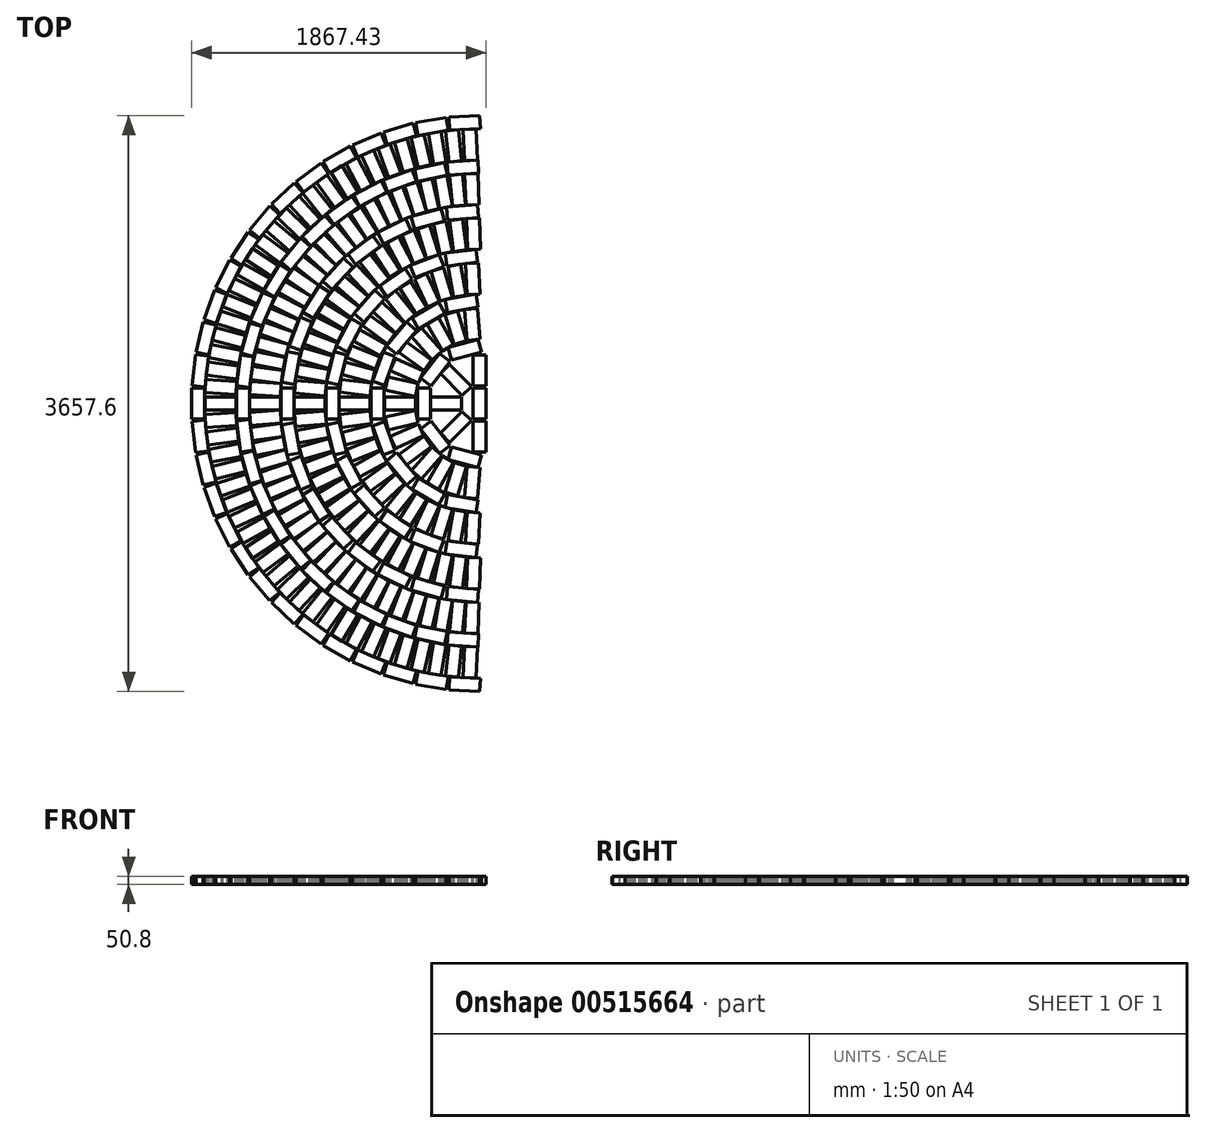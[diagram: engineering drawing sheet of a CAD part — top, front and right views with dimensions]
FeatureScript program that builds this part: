
annotation { "Feature Type Name" : "Feature", "Feature Type Description" : "" }
export const myFeature = defineFeature(function(context is Context, id is Id, definition is map)
    precondition{}
    {
        {
            var Q0;
            Q0=qCreatedBy(makeId("Top.planeOp"),FACE);
            var sketch = newSketch(context, id + "F0", { "sketchPlane" : qUnion([Q0])});
            skArc(sketch, "E0", {"start": v(0, 1828.8) * mm, "mid": v(-1828.8, 0) * mm, "end": v(0, -1828.8) * mm, "construction": true});
            skLineSegment(sketch, "E1", {"start": v(0, 1828.8) * mm, "end": v(0, -1828.8) * mm, "construction": true});
            skCircle(sketch, "E2", {"center": v(-914.4, 0) * mm, "radius": 279.4 * mm, "construction": true});
            skCircle(sketch, "E3", {"center": v(-914.4, 0) * mm, "radius": 609.6 * mm, "construction": true});
            skSolve(sketch);
        }
        {
            var Q0;
            Q0=qCreatedBy(makeId("Top.planeOp"),FACE);
            var sketch = newSketch(context, id + "F1", { "sketchPlane" : qUnion([Q0])});
            skLineSegment(sketch, "E4.bottom", {"start": v(-1826.15, 98.43) * mm, "end": v(-1730.9, 98.43) * mm});
            skLineSegment(sketch, "E4.top", {"start": v(-1826.15, -98.43) * mm, "end": v(-1730.9, -98.43) * mm});
            skLineSegment(sketch, "E4.left", {"start": v(-1826.15, 98.43) * mm, "end": v(-1826.15, -98.43) * mm});
            skLineSegment(sketch, "E4.right", {"start": v(-1730.9, 98.43) * mm, "end": v(-1730.9, -98.43) * mm});
            skLineSegment(sketch, "E5.1.0", {"start": v(-1802.2, 310.84) * mm, "end": v(-1825.16, 115.33) * mm});
            skLineSegment(sketch, "E5.1.1", {"start": v(-1802.2, 310.84) * mm, "end": v(-1707.6, 299.72) * mm});
            skLineSegment(sketch, "E5.1.2", {"start": v(-1707.6, 299.72) * mm, "end": v(-1730.56, 104.22) * mm});
            skLineSegment(sketch, "E5.1.3", {"start": v(-1825.16, 115.33) * mm, "end": v(-1730.56, 104.22) * mm});
            skLineSegment(sketch, "E5.2.0", {"start": v(-1753.6, 519) * mm, "end": v(-1799.23, 327.52) * mm});
            skLineSegment(sketch, "E5.2.1", {"start": v(-1753.6, 519) * mm, "end": v(-1660.95, 496.93) * mm});
            skLineSegment(sketch, "E5.2.2", {"start": v(-1660.95, 496.93) * mm, "end": v(-1706.58, 305.44) * mm});
            skLineSegment(sketch, "E5.2.3", {"start": v(-1799.23, 327.52) * mm, "end": v(-1706.58, 305.44) * mm});
            skLineSegment(sketch, "E5.3.0", {"start": v(-1681.07, 720.08) * mm, "end": v(-1748.73, 535.22) * mm});
            skLineSegment(sketch, "E5.3.1", {"start": v(-1681.07, 720.08) * mm, "end": v(-1591.62, 687.34) * mm});
            skLineSegment(sketch, "E5.3.2", {"start": v(-1591.62, 687.34) * mm, "end": v(-1659.28, 502.49) * mm});
            skLineSegment(sketch, "E5.3.3", {"start": v(-1748.73, 535.22) * mm, "end": v(-1659.28, 502.49) * mm});
            skLineSegment(sketch, "E5.4.0", {"start": v(-1585.56, 911.32) * mm, "end": v(-1674.33, 735.62) * mm});
            skLineSegment(sketch, "E5.4.1", {"start": v(-1585.56, 911.32) * mm, "end": v(-1500.55, 868.37) * mm});
            skLineSegment(sketch, "E5.4.2", {"start": v(-1500.55, 868.37) * mm, "end": v(-1589.31, 692.67) * mm});
            skLineSegment(sketch, "E5.4.3", {"start": v(-1674.33, 735.62) * mm, "end": v(-1589.31, 692.67) * mm});
            skLineSegment(sketch, "E5.5.0", {"start": v(-1468.4, 1090.1) * mm, "end": v(-1577.05, 925.96) * mm});
            skLineSegment(sketch, "E5.5.1", {"start": v(-1468.4, 1090.1) * mm, "end": v(-1388.97, 1037.53) * mm});
            skLineSegment(sketch, "E5.5.2", {"start": v(-1388.97, 1037.53) * mm, "end": v(-1497.63, 873.39) * mm});
            skLineSegment(sketch, "E5.5.3", {"start": v(-1577.05, 925.96) * mm, "end": v(-1497.63, 873.39) * mm});
            skLineSegment(sketch, "E5.6.0", {"start": v(-1331.16, 1254) * mm, "end": v(-1458.23, 1103.66) * mm});
            skLineSegment(sketch, "E5.6.1", {"start": v(-1331.16, 1254) * mm, "end": v(-1258.42, 1192.51) * mm});
            skLineSegment(sketch, "E5.6.2", {"start": v(-1258.42, 1192.51) * mm, "end": v(-1385.49, 1042.17) * mm});
            skLineSegment(sketch, "E5.6.3", {"start": v(-1458.23, 1103.66) * mm, "end": v(-1385.49, 1042.17) * mm});
            skLineSegment(sketch, "E5.7.0", {"start": v(-1175.75, 1400.76) * mm, "end": v(-1319.5, 1266.27) * mm});
            skLineSegment(sketch, "E5.7.1", {"start": v(-1175.75, 1400.76) * mm, "end": v(-1110.67, 1331.2) * mm});
            skLineSegment(sketch, "E5.7.2", {"start": v(-1110.67, 1331.2) * mm, "end": v(-1254.42, 1196.72) * mm});
            skLineSegment(sketch, "E5.7.3", {"start": v(-1319.5, 1266.27) * mm, "end": v(-1254.42, 1196.72) * mm});
            skLineSegment(sketch, "E5.8.0", {"start": v(-1004.27, 1528.38) * mm, "end": v(-1162.72, 1411.59) * mm});
            skLineSegment(sketch, "E5.8.1", {"start": v(-1004.27, 1528.38) * mm, "end": v(-947.75, 1451.71) * mm});
            skLineSegment(sketch, "E5.8.2", {"start": v(-947.75, 1451.71) * mm, "end": v(-1106.2, 1334.92) * mm});
            skLineSegment(sketch, "E5.8.3", {"start": v(-1162.72, 1411.59) * mm, "end": v(-1106.2, 1334.92) * mm});
            skLineSegment(sketch, "E5.9.0", {"start": v(-819.06, 1635.13) * mm, "end": v(-990.07, 1537.62) * mm});
            skLineSegment(sketch, "E5.9.1", {"start": v(-819.06, 1635.13) * mm, "end": v(-771.88, 1552.38) * mm});
            skLineSegment(sketch, "E5.9.2", {"start": v(-771.88, 1552.38) * mm, "end": v(-942.89, 1454.88) * mm});
            skLineSegment(sketch, "E5.9.3", {"start": v(-990.07, 1537.62) * mm, "end": v(-942.89, 1454.88) * mm});
            skLineSegment(sketch, "E5.10.0", {"start": v(-622.67, 1719.53) * mm, "end": v(-803.89, 1642.64) * mm});
            skLineSegment(sketch, "E5.10.1", {"start": v(-622.67, 1719.53) * mm, "end": v(-585.47, 1631.85) * mm});
            skLineSegment(sketch, "E5.10.2", {"start": v(-585.47, 1631.85) * mm, "end": v(-766.68, 1554.96) * mm});
            skLineSegment(sketch, "E5.10.3", {"start": v(-803.89, 1642.64) * mm, "end": v(-766.68, 1554.96) * mm});
            skLineSegment(sketch, "E5.11.0", {"start": v(-417.78, 1780.44) * mm, "end": v(-606.72, 1725.22) * mm});
            skLineSegment(sketch, "E5.11.1", {"start": v(-417.78, 1780.44) * mm, "end": v(-391.06, 1689.02) * mm});
            skLineSegment(sketch, "E5.11.2", {"start": v(-391.06, 1689.02) * mm, "end": v(-580, 1633.8) * mm});
            skLineSegment(sketch, "E5.11.3", {"start": v(-606.72, 1725.22) * mm, "end": v(-580, 1633.8) * mm});
            skLineSegment(sketch, "E5.12.0", {"start": v(-207.17, 1817.03) * mm, "end": v(-401.27, 1784.23) * mm});
            skLineSegment(sketch, "E5.12.1", {"start": v(-207.17, 1817.03) * mm, "end": v(-191.3, 1723.1) * mm});
            skLineSegment(sketch, "E5.12.2", {"start": v(-191.3, 1723.1) * mm, "end": v(-385.4, 1690.32) * mm});
            skLineSegment(sketch, "E5.12.3", {"start": v(-401.27, 1784.23) * mm, "end": v(-385.4, 1690.32) * mm});
            skLineSegment(sketch, "E5.13.0", {"start": v(6.27, 1828.79) * mm, "end": v(-190.33, 1818.87) * mm});
            skLineSegment(sketch, "E5.13.1", {"start": v(6.27, 1828.79) * mm, "end": v(11.07, 1733.66) * mm});
            skLineSegment(sketch, "E5.13.2", {"start": v(11.07, 1733.66) * mm, "end": v(-185.53, 1723.74) * mm});
            skLineSegment(sketch, "E5.13.3", {"start": v(-190.33, 1818.87) * mm, "end": v(-185.53, 1723.74) * mm});
            skPoint(sketch, "E5.center", {"position": v(0, 0) * mm});
            skLineSegment(sketch, "E5.anchor1", {"start": v(0, 0) * mm, "end": v(-1826.15, -98.43) * mm, "construction": true});
            skLineSegment(sketch, "E5.anchor2", {"start": v(0, 0) * mm, "end": v(-190.33, 1818.87) * mm, "construction": true});
            skLineSegment(sketch, "E6.MirrorCS", {"start": v(-1825.16, -115.33) * mm, "end": v(-1730.56, -104.22) * mm});
            skLineSegment(sketch, "E7.MirrorCS", {"start": v(-1802.2, -310.84) * mm, "end": v(-1825.16, -115.33) * mm});
            skLineSegment(sketch, "E8.MirrorCS", {"start": v(-1802.2, -310.84) * mm, "end": v(-1707.6, -299.72) * mm});
            skLineSegment(sketch, "E9.MirrorCS", {"start": v(-1707.6, -299.72) * mm, "end": v(-1730.56, -104.22) * mm});
            skLineSegment(sketch, "E10.MirrorCS", {"start": v(-190.33, -1818.87) * mm, "end": v(-185.53, -1723.74) * mm});
            skLineSegment(sketch, "E11.MirrorCS", {"start": v(-1826.15, -98.43) * mm, "end": v(-1826.15, 98.43) * mm});
            skLineSegment(sketch, "E12.MirrorCS", {"start": v(-1730.9, -98.43) * mm, "end": v(-1730.9, 98.43) * mm});
            skLineSegment(sketch, "E13.MirrorCS", {"start": v(-803.89, -1642.64) * mm, "end": v(-766.68, -1554.96) * mm});
            skLineSegment(sketch, "E14.MirrorCS", {"start": v(-990.07, -1537.62) * mm, "end": v(-942.89, -1454.88) * mm});
            skLineSegment(sketch, "E15.MirrorCS", {"start": v(-1681.07, -720.08) * mm, "end": v(-1591.62, -687.34) * mm});
            skLineSegment(sketch, "E16.MirrorCS", {"start": v(-1748.73, -535.22) * mm, "end": v(-1659.28, -502.49) * mm});
            skLineSegment(sketch, "E17.MirrorCS", {"start": v(-819.06, -1635.13) * mm, "end": v(-771.88, -1552.38) * mm});
            skLineSegment(sketch, "E18.MirrorCS", {"start": v(-191.3, -1723.1) * mm, "end": v(-385.4, -1690.32) * mm});
            skLineSegment(sketch, "E19.MirrorCS", {"start": v(-1458.23, -1103.66) * mm, "end": v(-1385.49, -1042.17) * mm});
            skLineSegment(sketch, "E20.MirrorCS", {"start": v(-207.17, -1817.03) * mm, "end": v(-191.3, -1723.1) * mm});
            skLineSegment(sketch, "E21.MirrorCS", {"start": v(-1175.75, -1400.76) * mm, "end": v(-1110.67, -1331.2) * mm});
            skLineSegment(sketch, "E22.MirrorCS", {"start": v(6.27, -1828.79) * mm, "end": v(-190.33, -1818.87) * mm});
            skLineSegment(sketch, "E23.MirrorCS", {"start": v(-1577.05, -925.96) * mm, "end": v(-1497.63, -873.39) * mm});
            skLineSegment(sketch, "E24.MirrorCS", {"start": v(-207.17, -1817.03) * mm, "end": v(-401.27, -1784.23) * mm});
            skLineSegment(sketch, "E25.MirrorCS", {"start": v(-606.72, -1725.22) * mm, "end": v(-580, -1633.8) * mm});
            skLineSegment(sketch, "E26.MirrorCS", {"start": v(-1004.27, -1528.38) * mm, "end": v(-1162.72, -1411.59) * mm});
            skLineSegment(sketch, "E27.MirrorCS", {"start": v(-1585.56, -911.32) * mm, "end": v(-1674.33, -735.62) * mm});
            skLineSegment(sketch, "E28.MirrorCS", {"start": v(-1331.16, -1254) * mm, "end": v(-1258.42, -1192.51) * mm});
            skLineSegment(sketch, "E29.MirrorCS", {"start": v(-1591.62, -687.34) * mm, "end": v(-1659.28, -502.49) * mm});
            skLineSegment(sketch, "E30.MirrorCS", {"start": v(-1468.4, -1090.1) * mm, "end": v(-1388.97, -1037.53) * mm});
            skLineSegment(sketch, "E31.MirrorCS", {"start": v(-1110.67, -1331.2) * mm, "end": v(-1254.42, -1196.72) * mm});
            skLineSegment(sketch, "E32.MirrorCS", {"start": v(-1331.16, -1254) * mm, "end": v(-1458.23, -1103.66) * mm});
            skLineSegment(sketch, "E33.MirrorCS", {"start": v(-1500.55, -868.37) * mm, "end": v(-1589.31, -692.67) * mm});
            skLineSegment(sketch, "E34.MirrorCS", {"start": v(-947.75, -1451.71) * mm, "end": v(-1106.2, -1334.92) * mm});
            skLineSegment(sketch, "E35.MirrorCS", {"start": v(-622.67, -1719.53) * mm, "end": v(-585.47, -1631.85) * mm});
            skLineSegment(sketch, "E36.MirrorCS", {"start": v(-1319.5, -1266.27) * mm, "end": v(-1254.42, -1196.72) * mm});
            skLineSegment(sketch, "E37.MirrorCS", {"start": v(-1388.97, -1037.53) * mm, "end": v(-1497.63, -873.39) * mm});
            skLineSegment(sketch, "E38.MirrorCS", {"start": v(-1258.42, -1192.51) * mm, "end": v(-1385.49, -1042.17) * mm});
            skLineSegment(sketch, "E39.MirrorCS", {"start": v(-585.47, -1631.85) * mm, "end": v(-766.68, -1554.96) * mm});
            skLineSegment(sketch, "E40.MirrorCS", {"start": v(-1799.23, -327.52) * mm, "end": v(-1706.58, -305.44) * mm});
            skLineSegment(sketch, "E41.MirrorCS", {"start": v(-771.88, -1552.38) * mm, "end": v(-942.89, -1454.88) * mm});
            skLineSegment(sketch, "E42.MirrorCS", {"start": v(-417.78, -1780.44) * mm, "end": v(-391.06, -1689.02) * mm});
            skLineSegment(sketch, "E43.MirrorCS", {"start": v(-1660.95, -496.93) * mm, "end": v(-1706.58, -305.44) * mm});
            skLineSegment(sketch, "E44.MirrorCS", {"start": v(-1468.4, -1090.1) * mm, "end": v(-1577.05, -925.96) * mm});
            skLineSegment(sketch, "E45.MirrorCS", {"start": v(-1753.6, -519) * mm, "end": v(-1660.95, -496.93) * mm});
            skLineSegment(sketch, "E46.MirrorCS", {"start": v(-819.06, -1635.13) * mm, "end": v(-990.07, -1537.62) * mm});
            skLineSegment(sketch, "E47.MirrorCS", {"start": v(-1162.72, -1411.59) * mm, "end": v(-1106.2, -1334.92) * mm});
            skLineSegment(sketch, "E48.MirrorCS", {"start": v(-1681.07, -720.08) * mm, "end": v(-1748.73, -535.22) * mm});
            skLineSegment(sketch, "E49.MirrorCS", {"start": v(-1674.33, -735.62) * mm, "end": v(-1589.31, -692.67) * mm});
            skLineSegment(sketch, "E50.MirrorCS", {"start": v(-1753.6, -519) * mm, "end": v(-1799.23, -327.52) * mm});
            skLineSegment(sketch, "E51.MirrorCS", {"start": v(-1175.75, -1400.76) * mm, "end": v(-1319.5, -1266.27) * mm});
            skLineSegment(sketch, "E52.MirrorCS", {"start": v(-1585.56, -911.32) * mm, "end": v(-1500.55, -868.37) * mm});
            skLineSegment(sketch, "E53.MirrorCS", {"start": v(-417.78, -1780.44) * mm, "end": v(-606.72, -1725.22) * mm});
            skLineSegment(sketch, "E54.MirrorCS", {"start": v(-1004.27, -1528.38) * mm, "end": v(-947.75, -1451.71) * mm});
            skLineSegment(sketch, "E55.MirrorCS", {"start": v(6.27, -1828.79) * mm, "end": v(11.07, -1733.66) * mm});
            skLineSegment(sketch, "E56.MirrorCS", {"start": v(-622.67, -1719.53) * mm, "end": v(-803.89, -1642.64) * mm});
            skLineSegment(sketch, "E57.MirrorCS", {"start": v(-401.27, -1784.23) * mm, "end": v(-385.4, -1690.32) * mm});
            skLineSegment(sketch, "E58.MirrorCS", {"start": v(-391.06, -1689.02) * mm, "end": v(-580, -1633.8) * mm});
            skLineSegment(sketch, "E59.MirrorCS", {"start": v(11.07, -1733.66) * mm, "end": v(-185.53, -1723.74) * mm});
            skLineSegment(sketch, "E60.MirrorCS", {"start": v(0, 0) * mm, "end": v(-190.33, -1818.87) * mm, "construction": true});
            skSolve(sketch);
        }
        {
            var Q0;
            Q0=qCreatedBy(makeId("Top.planeOp"),FACE);
            var sketch = newSketch(context, id + "F2", { "sketchPlane" : qUnion([Q0])});
            skCircle(sketch, "E61", {"center": v(0, 0) * mm, "radius": 1730.9 * mm, "construction": true});
            skLineSegment(sketch, "E62.bottom", {"start": v(-1730.24, 47.63) * mm, "end": v(-1533.4, 47.63) * mm});
            skLineSegment(sketch, "E62.top", {"start": v(-1730.24, -47.63) * mm, "end": v(-1533.4, -47.63) * mm});
            skLineSegment(sketch, "E62.left", {"start": v(-1730.24, 47.63) * mm, "end": v(-1730.24, -47.63) * mm});
            skLineSegment(sketch, "E62.right", {"start": v(-1533.4, 47.63) * mm, "end": v(-1533.4, -47.63) * mm});
            skLineSegment(sketch, "E63.1.0", {"start": v(-1723.66, 158.1) * mm, "end": v(-1527.22, 145.51) * mm});
            skLineSegment(sketch, "E63.1.1", {"start": v(-1527.22, 145.51) * mm, "end": v(-1533.3, 50.46) * mm});
            skLineSegment(sketch, "E63.1.2", {"start": v(-1729.75, 63.04) * mm, "end": v(-1533.3, 50.46) * mm});
            skLineSegment(sketch, "E63.1.3", {"start": v(-1723.66, 158.1) * mm, "end": v(-1729.75, 63.04) * mm});
            skLineSegment(sketch, "E63.2.0", {"start": v(-1710.04, 267.92) * mm, "end": v(-1514.8, 242.8) * mm});
            skLineSegment(sketch, "E63.2.1", {"start": v(-1514.8, 242.8) * mm, "end": v(-1526.95, 148.34) * mm});
            skLineSegment(sketch, "E63.2.2", {"start": v(-1722.19, 173.44) * mm, "end": v(-1526.95, 148.34) * mm});
            skLineSegment(sketch, "E63.2.3", {"start": v(-1710.04, 267.92) * mm, "end": v(-1722.19, 173.44) * mm});
            skLineSegment(sketch, "E63.3.0", {"start": v(-1689.42, 376.64) * mm, "end": v(-1496.18, 339.11) * mm});
            skLineSegment(sketch, "E63.3.1", {"start": v(-1496.18, 339.11) * mm, "end": v(-1514.35, 245.6) * mm});
            skLineSegment(sketch, "E63.3.2", {"start": v(-1707.58, 283.14) * mm, "end": v(-1514.35, 245.6) * mm});
            skLineSegment(sketch, "E63.3.3", {"start": v(-1689.42, 376.64) * mm, "end": v(-1707.58, 283.14) * mm});
            skLineSegment(sketch, "E63.4.0", {"start": v(-1661.9, 483.83) * mm, "end": v(-1471.46, 434.03) * mm});
            skLineSegment(sketch, "E63.4.1", {"start": v(-1471.46, 434.03) * mm, "end": v(-1495.56, 341.88) * mm});
            skLineSegment(sketch, "E63.4.2", {"start": v(-1686, 391.68) * mm, "end": v(-1495.56, 341.88) * mm});
            skLineSegment(sketch, "E63.4.3", {"start": v(-1661.9, 483.83) * mm, "end": v(-1686, 391.68) * mm});
            skLineSegment(sketch, "E63.5.0", {"start": v(-1627.59, 589.04) * mm, "end": v(-1440.71, 527.17) * mm});
            skLineSegment(sketch, "E63.5.1", {"start": v(-1440.71, 527.17) * mm, "end": v(-1470.65, 436.75) * mm});
            skLineSegment(sketch, "E63.5.2", {"start": v(-1657.53, 498.62) * mm, "end": v(-1470.65, 436.75) * mm});
            skLineSegment(sketch, "E63.5.3", {"start": v(-1627.59, 589.04) * mm, "end": v(-1657.53, 498.62) * mm});
            skLineSegment(sketch, "E63.6.0", {"start": v(-1586.62, 691.84) * mm, "end": v(-1404.08, 618.16) * mm});
            skLineSegment(sketch, "E63.6.1", {"start": v(-1404.08, 618.16) * mm, "end": v(-1439.74, 529.83) * mm});
            skLineSegment(sketch, "E63.6.2", {"start": v(-1622.28, 603.52) * mm, "end": v(-1439.74, 529.83) * mm});
            skLineSegment(sketch, "E63.6.3", {"start": v(-1586.62, 691.84) * mm, "end": v(-1622.28, 603.52) * mm});
            skLineSegment(sketch, "E63.7.0", {"start": v(-1539.17, 791.82) * mm, "end": v(-1361.71, 706.62) * mm});
            skLineSegment(sketch, "E63.7.1", {"start": v(-1361.71, 706.62) * mm, "end": v(-1402.94, 620.75) * mm});
            skLineSegment(sketch, "E63.7.2", {"start": v(-1580.4, 705.95) * mm, "end": v(-1402.94, 620.75) * mm});
            skLineSegment(sketch, "E63.7.3", {"start": v(-1539.17, 791.82) * mm, "end": v(-1580.4, 705.95) * mm});
            skLineSegment(sketch, "E63.8.0", {"start": v(-1485.42, 888.55) * mm, "end": v(-1313.77, 792.19) * mm});
            skLineSegment(sketch, "E63.8.1", {"start": v(-1313.77, 792.19) * mm, "end": v(-1360.4, 709.13) * mm});
            skLineSegment(sketch, "E63.8.2", {"start": v(-1532.05, 805.5) * mm, "end": v(-1360.4, 709.13) * mm});
            skLineSegment(sketch, "E63.8.3", {"start": v(-1485.42, 888.55) * mm, "end": v(-1532.05, 805.5) * mm});
            skLineSegment(sketch, "E63.9.0", {"start": v(-1425.6, 981.66) * mm, "end": v(-1260.47, 874.52) * mm});
            skLineSegment(sketch, "E63.9.1", {"start": v(-1260.47, 874.52) * mm, "end": v(-1312.3, 794.62) * mm});
            skLineSegment(sketch, "E63.9.2", {"start": v(-1477.45, 901.75) * mm, "end": v(-1312.3, 794.62) * mm});
            skLineSegment(sketch, "E63.9.3", {"start": v(-1425.6, 981.66) * mm, "end": v(-1477.45, 901.75) * mm});
            skLineSegment(sketch, "E63.10.0", {"start": v(-1359.96, 1070.75) * mm, "end": v(-1202, 953.28) * mm});
            skLineSegment(sketch, "E63.10.1", {"start": v(-1202, 953.28) * mm, "end": v(-1258.85, 876.85) * mm});
            skLineSegment(sketch, "E63.10.2", {"start": v(-1416.8, 994.32) * mm, "end": v(-1258.85, 876.85) * mm});
            skLineSegment(sketch, "E63.10.3", {"start": v(-1359.96, 1070.75) * mm, "end": v(-1416.8, 994.32) * mm});
            skLineSegment(sketch, "E63.11.0", {"start": v(-1288.76, 1155.47) * mm, "end": v(-1138.63, 1028.14) * mm});
            skLineSegment(sketch, "E63.11.1", {"start": v(-1138.63, 1028.14) * mm, "end": v(-1200.24, 955.5) * mm});
            skLineSegment(sketch, "E63.11.2", {"start": v(-1350.37, 1082.83) * mm, "end": v(-1200.24, 955.5) * mm});
            skLineSegment(sketch, "E63.11.3", {"start": v(-1288.76, 1155.47) * mm, "end": v(-1350.37, 1082.83) * mm});
            skLineSegment(sketch, "E63.12.0", {"start": v(-1212.3, 1235.46) * mm, "end": v(-1070.6, 1098.8) * mm});
            skLineSegment(sketch, "E63.12.1", {"start": v(-1070.6, 1098.8) * mm, "end": v(-1136.73, 1030.25) * mm});
            skLineSegment(sketch, "E63.12.2", {"start": v(-1278.42, 1166.9) * mm, "end": v(-1136.73, 1030.25) * mm});
            skLineSegment(sketch, "E63.12.3", {"start": v(-1212.3, 1235.46) * mm, "end": v(-1278.42, 1166.9) * mm});
            skLineSegment(sketch, "E63.13.0", {"start": v(-1130.86, 1310.4) * mm, "end": v(-998.2, 1164.97) * mm});
            skLineSegment(sketch, "E63.13.1", {"start": v(-998.2, 1164.97) * mm, "end": v(-1068.57, 1100.78) * mm});
            skLineSegment(sketch, "E63.13.2", {"start": v(-1201.24, 1246.21) * mm, "end": v(-1068.57, 1100.78) * mm});
            skLineSegment(sketch, "E63.13.3", {"start": v(-1130.86, 1310.4) * mm, "end": v(-1201.24, 1246.21) * mm});
            skLineSegment(sketch, "E63.14.0", {"start": v(-1044.82, 1380) * mm, "end": v(-921.72, 1226.38) * mm});
            skLineSegment(sketch, "E63.14.1", {"start": v(-921.72, 1226.38) * mm, "end": v(-996.05, 1166.81) * mm});
            skLineSegment(sketch, "E63.14.2", {"start": v(-1119.14, 1320.43) * mm, "end": v(-996.05, 1166.81) * mm});
            skLineSegment(sketch, "E63.14.3", {"start": v(-1044.82, 1380) * mm, "end": v(-1119.14, 1320.43) * mm});
            skLineSegment(sketch, "E63.15.0", {"start": v(-954.5, 1443.94) * mm, "end": v(-841.47, 1282.77) * mm});
            skLineSegment(sketch, "E63.15.1", {"start": v(-841.47, 1282.77) * mm, "end": v(-919.45, 1228.08) * mm});
            skLineSegment(sketch, "E63.15.2", {"start": v(-1032.48, 1389.24) * mm, "end": v(-919.45, 1228.08) * mm});
            skLineSegment(sketch, "E63.15.3", {"start": v(-954.5, 1443.94) * mm, "end": v(-1032.48, 1389.24) * mm});
            skLineSegment(sketch, "E63.16.0", {"start": v(-860.27, 1501.98) * mm, "end": v(-757.78, 1333.92) * mm});
            skLineSegment(sketch, "E63.16.1", {"start": v(-757.78, 1333.92) * mm, "end": v(-839.1, 1284.32) * mm});
            skLineSegment(sketch, "E63.16.2", {"start": v(-941.6, 1452.38) * mm, "end": v(-839.1, 1284.32) * mm});
            skLineSegment(sketch, "E63.16.3", {"start": v(-860.27, 1501.98) * mm, "end": v(-941.6, 1452.38) * mm});
            skLineSegment(sketch, "E63.17.0", {"start": v(-762.54, 1553.88) * mm, "end": v(-670.99, 1379.62) * mm});
            skLineSegment(sketch, "E63.17.1", {"start": v(-670.99, 1379.62) * mm, "end": v(-755.3, 1335.32) * mm});
            skLineSegment(sketch, "E63.17.2", {"start": v(-846.86, 1509.58) * mm, "end": v(-755.3, 1335.32) * mm});
            skLineSegment(sketch, "E63.17.3", {"start": v(-762.54, 1553.88) * mm, "end": v(-846.86, 1509.58) * mm});
            skLineSegment(sketch, "E63.18.0", {"start": v(-661.68, 1599.43) * mm, "end": v(-581.46, 1419.67) * mm});
            skLineSegment(sketch, "E63.18.1", {"start": v(-581.46, 1419.67) * mm, "end": v(-668.44, 1380.85) * mm});
            skLineSegment(sketch, "E63.18.2", {"start": v(-748.66, 1560.61) * mm, "end": v(-668.44, 1380.85) * mm});
            skLineSegment(sketch, "E63.18.3", {"start": v(-661.68, 1599.43) * mm, "end": v(-748.66, 1560.61) * mm});
            skLineSegment(sketch, "E63.19.0", {"start": v(-558.12, 1638.45) * mm, "end": v(-489.55, 1453.93) * mm});
            skLineSegment(sketch, "E63.19.1", {"start": v(-489.55, 1453.93) * mm, "end": v(-578.83, 1420.75) * mm});
            skLineSegment(sketch, "E63.19.2", {"start": v(-647.4, 1605.27) * mm, "end": v(-578.83, 1420.75) * mm});
            skLineSegment(sketch, "E63.19.3", {"start": v(-558.12, 1638.45) * mm, "end": v(-647.4, 1605.27) * mm});
            skLineSegment(sketch, "E63.20.0", {"start": v(-452.28, 1670.76) * mm, "end": v(-395.64, 1482.24) * mm});
            skLineSegment(sketch, "E63.20.1", {"start": v(-395.64, 1482.24) * mm, "end": v(-486.86, 1454.83) * mm});
            skLineSegment(sketch, "E63.20.2", {"start": v(-543.5, 1643.36) * mm, "end": v(-486.86, 1454.83) * mm});
            skLineSegment(sketch, "E63.20.3", {"start": v(-452.28, 1670.76) * mm, "end": v(-543.5, 1643.36) * mm});
            skLineSegment(sketch, "E63.21.0", {"start": v(-344.6, 1696.25) * mm, "end": v(-300.11, 1504.5) * mm});
            skLineSegment(sketch, "E63.21.1", {"start": v(-300.11, 1504.5) * mm, "end": v(-392.9, 1482.97) * mm});
            skLineSegment(sketch, "E63.21.2", {"start": v(-437.38, 1674.73) * mm, "end": v(-392.9, 1482.97) * mm});
            skLineSegment(sketch, "E63.21.3", {"start": v(-344.6, 1696.25) * mm, "end": v(-437.38, 1674.73) * mm});
            skLineSegment(sketch, "E63.22.0", {"start": v(-235.5, 1714.8) * mm, "end": v(-203.36, 1520.6) * mm});
            skLineSegment(sketch, "E63.22.1", {"start": v(-203.36, 1520.6) * mm, "end": v(-297.33, 1505.05) * mm});
            skLineSegment(sketch, "E63.22.2", {"start": v(-329.47, 1699.25) * mm, "end": v(-297.33, 1505.05) * mm});
            skLineSegment(sketch, "E63.22.3", {"start": v(-235.5, 1714.8) * mm, "end": v(-329.47, 1699.25) * mm});
            skLineSegment(sketch, "E63.23.0", {"start": v(-125.43, 1726.35) * mm, "end": v(-105.77, 1530.48) * mm});
            skLineSegment(sketch, "E63.23.1", {"start": v(-105.77, 1530.48) * mm, "end": v(-200.55, 1520.97) * mm});
            skLineSegment(sketch, "E63.23.2", {"start": v(-220.2, 1716.83) * mm, "end": v(-200.55, 1520.97) * mm});
            skLineSegment(sketch, "E63.23.3", {"start": v(-125.43, 1726.35) * mm, "end": v(-220.2, 1716.83) * mm});
            skLineSegment(sketch, "E63.24.0", {"start": v(-14.86, 1730.84) * mm, "end": v(-7.76, 1534.11) * mm});
            skLineSegment(sketch, "E63.24.1", {"start": v(-7.76, 1534.11) * mm, "end": v(-102.94, 1530.68) * mm});
            skLineSegment(sketch, "E63.24.2", {"start": v(-110.05, 1727.4) * mm, "end": v(-102.94, 1530.68) * mm});
            skLineSegment(sketch, "E63.24.3", {"start": v(-14.86, 1730.84) * mm, "end": v(-110.05, 1727.4) * mm});
            skLineSegment(sketch, "E63.anchor1", {"start": v(0, 0) * mm, "end": v(-1730.24, 47.63) * mm, "construction": true});
            skLineSegment(sketch, "E63.anchor2", {"start": v(0, 0) * mm, "end": v(-14.86, 1730.84) * mm, "construction": true});
            skLineSegment(sketch, "E64.MirrorCS", {"start": v(-1729.75, -63.04) * mm, "end": v(-1533.3, -50.46) * mm});
            skLineSegment(sketch, "E65.MirrorCS", {"start": v(-1723.66, -158.1) * mm, "end": v(-1729.75, -63.04) * mm});
            skLineSegment(sketch, "E66.MirrorCS", {"start": v(-1723.66, -158.1) * mm, "end": v(-1527.22, -145.51) * mm});
            skLineSegment(sketch, "E67.MirrorCS", {"start": v(-1527.22, -145.51) * mm, "end": v(-1533.3, -50.46) * mm});
            skLineSegment(sketch, "E68.MirrorCS", {"start": v(-1359.96, -1070.75) * mm, "end": v(-1416.8, -994.32) * mm});
            skLineSegment(sketch, "E69.MirrorCS", {"start": v(-1361.71, -706.62) * mm, "end": v(-1402.94, -620.75) * mm});
            skLineSegment(sketch, "E70.MirrorCS", {"start": v(-1425.6, -981.66) * mm, "end": v(-1260.47, -874.52) * mm});
            skLineSegment(sketch, "E71.MirrorCS", {"start": v(-105.77, -1530.48) * mm, "end": v(-200.55, -1520.97) * mm});
            skLineSegment(sketch, "E72.MirrorCS", {"start": v(-1440.71, -527.17) * mm, "end": v(-1470.65, -436.75) * mm});
            skLineSegment(sketch, "E73.MirrorCS", {"start": v(-300.11, -1504.5) * mm, "end": v(-392.9, -1482.97) * mm});
            skLineSegment(sketch, "E74.MirrorCS", {"start": v(-670.99, -1379.62) * mm, "end": v(-755.3, -1335.32) * mm});
            skLineSegment(sketch, "E75.MirrorCS", {"start": v(-998.2, -1164.97) * mm, "end": v(-1068.57, -1100.78) * mm});
            skLineSegment(sketch, "E76.MirrorCS", {"start": v(-1260.47, -874.52) * mm, "end": v(-1312.3, -794.62) * mm});
            skLineSegment(sketch, "E77.MirrorCS", {"start": v(-1539.17, -791.82) * mm, "end": v(-1580.4, -705.95) * mm});
            skLineSegment(sketch, "E78.MirrorCS", {"start": v(-125.43, -1726.35) * mm, "end": v(-220.2, -1716.83) * mm});
            skLineSegment(sketch, "E79.MirrorCS", {"start": v(-1689.42, -376.64) * mm, "end": v(-1707.58, -283.14) * mm});
            skLineSegment(sketch, "E80.MirrorCS", {"start": v(-1425.6, -981.66) * mm, "end": v(-1477.45, -901.75) * mm});
            skLineSegment(sketch, "E81.MirrorCS", {"start": v(-1496.18, -339.11) * mm, "end": v(-1514.35, -245.6) * mm});
            skLineSegment(sketch, "E82.MirrorCS", {"start": v(-1471.46, -434.03) * mm, "end": v(-1495.56, -341.88) * mm});
            skLineSegment(sketch, "E83.MirrorCS", {"start": v(-757.78, -1333.92) * mm, "end": v(-839.1, -1284.32) * mm});
            skLineSegment(sketch, "E84.MirrorCS", {"start": v(-1313.77, -792.19) * mm, "end": v(-1360.4, -709.13) * mm});
            skLineSegment(sketch, "E85.MirrorCS", {"start": v(-1514.8, -242.8) * mm, "end": v(-1526.95, -148.34) * mm});
            skLineSegment(sketch, "E86.MirrorCS", {"start": v(-1404.08, -618.16) * mm, "end": v(-1439.74, -529.83) * mm});
            skLineSegment(sketch, "E87.MirrorCS", {"start": v(-203.36, -1520.6) * mm, "end": v(-297.33, -1505.05) * mm});
            skLineSegment(sketch, "E88.MirrorCS", {"start": v(-581.46, -1419.67) * mm, "end": v(-668.44, -1380.85) * mm});
            skLineSegment(sketch, "E89.MirrorCS", {"start": v(-1661.9, -483.83) * mm, "end": v(-1686, -391.68) * mm});
            skLineSegment(sketch, "E90.MirrorCS", {"start": v(-1212.3, -1235.46) * mm, "end": v(-1278.42, -1166.9) * mm});
            skLineSegment(sketch, "E91.MirrorCS", {"start": v(-1485.42, -888.55) * mm, "end": v(-1532.05, -805.5) * mm});
            skLineSegment(sketch, "E92.MirrorCS", {"start": v(-14.86, -1730.84) * mm, "end": v(-110.05, -1727.4) * mm});
            skLineSegment(sketch, "E93.MirrorCS", {"start": v(-1201.24, -1246.21) * mm, "end": v(-1068.57, -1100.78) * mm});
            skLineSegment(sketch, "E94.MirrorCS", {"start": v(-1044.82, -1380) * mm, "end": v(-1119.14, -1320.43) * mm});
            skLineSegment(sketch, "E95.MirrorCS", {"start": v(-1586.62, -691.84) * mm, "end": v(-1622.28, -603.52) * mm});
            skLineSegment(sketch, "E96.MirrorCS", {"start": v(-235.5, -1714.8) * mm, "end": v(-329.47, -1699.25) * mm});
            skLineSegment(sketch, "E97.MirrorCS", {"start": v(-661.68, -1599.43) * mm, "end": v(-748.66, -1560.61) * mm});
            skLineSegment(sketch, "E98.MirrorCS", {"start": v(-489.55, -1453.93) * mm, "end": v(-578.83, -1420.75) * mm});
            skLineSegment(sketch, "E99.MirrorCS", {"start": v(-841.47, -1282.77) * mm, "end": v(-919.45, -1228.08) * mm});
            skLineSegment(sketch, "E100.MirrorCS", {"start": v(-1138.63, -1028.14) * mm, "end": v(-1200.24, -955.5) * mm});
            skLineSegment(sketch, "E101.MirrorCS", {"start": v(-558.12, -1638.45) * mm, "end": v(-647.4, -1605.27) * mm});
            skLineSegment(sketch, "E102.MirrorCS", {"start": v(-954.5, -1443.94) * mm, "end": v(-1032.48, -1389.24) * mm});
            skLineSegment(sketch, "E103.MirrorCS", {"start": v(-1288.76, -1155.47) * mm, "end": v(-1350.37, -1082.83) * mm});
            skLineSegment(sketch, "E104.MirrorCS", {"start": v(-1130.86, -1310.4) * mm, "end": v(-1201.24, -1246.21) * mm});
            skLineSegment(sketch, "E105.MirrorCS", {"start": v(-1627.59, -589.04) * mm, "end": v(-1657.53, -498.62) * mm});
            skLineSegment(sketch, "E106.MirrorCS", {"start": v(-344.6, -1696.25) * mm, "end": v(-437.38, -1674.73) * mm});
            skLineSegment(sketch, "E107.MirrorCS", {"start": v(-762.54, -1553.88) * mm, "end": v(-846.86, -1509.58) * mm});
            skLineSegment(sketch, "E108.MirrorCS", {"start": v(-1212.3, -1235.46) * mm, "end": v(-1070.6, -1098.8) * mm});
            skLineSegment(sketch, "E109.MirrorCS", {"start": v(-395.64, -1482.24) * mm, "end": v(-486.86, -1454.83) * mm});
            skLineSegment(sketch, "E110.MirrorCS", {"start": v(-1070.6, -1098.8) * mm, "end": v(-1136.73, -1030.25) * mm});
            skLineSegment(sketch, "E111.MirrorCS", {"start": v(-7.76, -1534.11) * mm, "end": v(-102.94, -1530.68) * mm});
            skLineSegment(sketch, "E112.MirrorCS", {"start": v(-1710.04, -267.92) * mm, "end": v(-1722.19, -173.44) * mm});
            skLineSegment(sketch, "E113.MirrorCS", {"start": v(-921.72, -1226.38) * mm, "end": v(-996.05, -1166.81) * mm});
            skLineSegment(sketch, "E114.MirrorCS", {"start": v(-1202, -953.28) * mm, "end": v(-1258.85, -876.85) * mm});
            skLineSegment(sketch, "E115.MirrorCS", {"start": v(-1278.42, -1166.9) * mm, "end": v(-1136.73, -1030.25) * mm});
            skLineSegment(sketch, "E116.MirrorCS", {"start": v(-452.28, -1670.76) * mm, "end": v(-543.5, -1643.36) * mm});
            skLineSegment(sketch, "E117.MirrorCS", {"start": v(-860.27, -1501.98) * mm, "end": v(-941.6, -1452.38) * mm});
            skLineSegment(sketch, "E118.MirrorCS", {"start": v(-1288.76, -1155.47) * mm, "end": v(-1138.63, -1028.14) * mm});
            skLineSegment(sketch, "E119.MirrorCS", {"start": v(-762.54, -1553.88) * mm, "end": v(-670.99, -1379.62) * mm});
            skLineSegment(sketch, "E120.MirrorCS", {"start": v(-1130.86, -1310.4) * mm, "end": v(-998.2, -1164.97) * mm});
            skLineSegment(sketch, "E121.MirrorCS", {"start": v(-647.4, -1605.27) * mm, "end": v(-578.83, -1420.75) * mm});
            skLineSegment(sketch, "E122.MirrorCS", {"start": v(-1032.48, -1389.24) * mm, "end": v(-919.45, -1228.08) * mm});
            skLineSegment(sketch, "E123.MirrorCS", {"start": v(-1350.37, -1082.83) * mm, "end": v(-1200.24, -955.5) * mm});
            skLineSegment(sketch, "E124.MirrorCS", {"start": v(-220.2, -1716.83) * mm, "end": v(-200.55, -1520.97) * mm});
            skLineSegment(sketch, "E125.MirrorCS", {"start": v(-1657.53, -498.62) * mm, "end": v(-1470.65, -436.75) * mm});
            skLineSegment(sketch, "E126.MirrorCS", {"start": v(-14.86, -1730.84) * mm, "end": v(-7.76, -1534.11) * mm});
            skLineSegment(sketch, "E127.MirrorCS", {"start": v(-1689.42, -376.64) * mm, "end": v(-1496.18, -339.11) * mm});
            skLineSegment(sketch, "E128.MirrorCS", {"start": v(-941.6, -1452.38) * mm, "end": v(-839.1, -1284.32) * mm});
            skLineSegment(sketch, "E129.MirrorCS", {"start": v(-110.05, -1727.4) * mm, "end": v(-102.94, -1530.68) * mm});
            skLineSegment(sketch, "E130.MirrorCS", {"start": v(-1627.59, -589.04) * mm, "end": v(-1440.71, -527.17) * mm});
            skLineSegment(sketch, "E131.MirrorCS", {"start": v(-344.6, -1696.25) * mm, "end": v(-300.11, -1504.5) * mm});
            skLineSegment(sketch, "E132.MirrorCS", {"start": v(-1580.4, -705.95) * mm, "end": v(-1402.94, -620.75) * mm});
            skLineSegment(sketch, "E133.MirrorCS", {"start": v(0, 0) * mm, "end": v(-14.86, -1730.84) * mm, "construction": true});
            skLineSegment(sketch, "E134.MirrorCS", {"start": v(-1477.45, -901.75) * mm, "end": v(-1312.3, -794.62) * mm});
            skLineSegment(sketch, "E135.MirrorCS", {"start": v(-437.38, -1674.73) * mm, "end": v(-392.9, -1482.97) * mm});
            skLineSegment(sketch, "E136.MirrorCS", {"start": v(-846.86, -1509.58) * mm, "end": v(-755.3, -1335.32) * mm});
            skLineSegment(sketch, "E137.MirrorCS", {"start": v(-1661.9, -483.83) * mm, "end": v(-1471.46, -434.03) * mm});
            skLineSegment(sketch, "E138.MirrorCS", {"start": v(-452.28, -1670.76) * mm, "end": v(-395.64, -1482.24) * mm});
            skLineSegment(sketch, "E139.MirrorCS", {"start": v(-860.27, -1501.98) * mm, "end": v(-757.78, -1333.92) * mm});
            skLineSegment(sketch, "E140.MirrorCS", {"start": v(-1485.42, -888.55) * mm, "end": v(-1313.77, -792.19) * mm});
            skLineSegment(sketch, "E141.MirrorCS", {"start": v(-1044.82, -1380) * mm, "end": v(-921.72, -1226.38) * mm});
            skLineSegment(sketch, "E142.MirrorCS", {"start": v(-1359.96, -1070.75) * mm, "end": v(-1202, -953.28) * mm});
            skLineSegment(sketch, "E143.MirrorCS", {"start": v(-1586.62, -691.84) * mm, "end": v(-1404.08, -618.16) * mm});
            skLineSegment(sketch, "E144.MirrorCS", {"start": v(-235.5, -1714.8) * mm, "end": v(-203.36, -1520.6) * mm});
            skLineSegment(sketch, "E145.MirrorCS", {"start": v(-661.68, -1599.43) * mm, "end": v(-581.46, -1419.67) * mm});
            skLineSegment(sketch, "E146.MirrorCS", {"start": v(-1707.58, -283.14) * mm, "end": v(-1514.35, -245.6) * mm});
            skLineSegment(sketch, "E147.MirrorCS", {"start": v(-1710.04, -267.92) * mm, "end": v(-1514.8, -242.8) * mm});
            skLineSegment(sketch, "E148.MirrorCS", {"start": v(-1722.19, -173.44) * mm, "end": v(-1526.95, -148.34) * mm});
            skLineSegment(sketch, "E149.MirrorCS", {"start": v(-1686, -391.68) * mm, "end": v(-1495.56, -341.88) * mm});
            skLineSegment(sketch, "E150.MirrorCS", {"start": v(-543.5, -1643.36) * mm, "end": v(-486.86, -1454.83) * mm});
            skLineSegment(sketch, "E151.MirrorCS", {"start": v(-1532.05, -805.5) * mm, "end": v(-1360.4, -709.13) * mm});
            skLineSegment(sketch, "E152.MirrorCS", {"start": v(-1119.14, -1320.43) * mm, "end": v(-996.05, -1166.81) * mm});
            skLineSegment(sketch, "E153.MirrorCS", {"start": v(-1416.8, -994.32) * mm, "end": v(-1258.85, -876.85) * mm});
            skLineSegment(sketch, "E154.MirrorCS", {"start": v(-1622.28, -603.52) * mm, "end": v(-1439.74, -529.83) * mm});
            skLineSegment(sketch, "E155.MirrorCS", {"start": v(-329.47, -1699.25) * mm, "end": v(-297.33, -1505.05) * mm});
            skLineSegment(sketch, "E156.MirrorCS", {"start": v(-748.66, -1560.61) * mm, "end": v(-668.44, -1380.85) * mm});
            skLineSegment(sketch, "E157.MirrorCS", {"start": v(-558.12, -1638.45) * mm, "end": v(-489.55, -1453.93) * mm});
            skLineSegment(sketch, "E158.MirrorCS", {"start": v(-954.5, -1443.94) * mm, "end": v(-841.47, -1282.77) * mm});
            skLineSegment(sketch, "E159.MirrorCS", {"start": v(-1539.17, -791.82) * mm, "end": v(-1361.71, -706.62) * mm});
            skLineSegment(sketch, "E160.MirrorCS", {"start": v(-125.43, -1726.35) * mm, "end": v(-105.77, -1530.48) * mm});
            skSolve(sketch);
        }
        {
            var Q0;
            Q0=qCreatedBy(makeId("Top.planeOp"),FACE);
            var sketch = newSketch(context, id + "F3", { "sketchPlane" : qUnion([Q0])});
            skArc(sketch, "E161", {"start": v(-8.56, 1533.37) * mm, "mid": v(-1533.4, 0) * mm, "end": v(-8.56, -1533.37) * mm});
            skLineSegment(sketch, "E162.bottom", {"start": v(-1434.98, 98.43) * mm, "end": v(-1530.23, 98.43) * mm});
            skLineSegment(sketch, "E162.top", {"start": v(-1434.98, -98.43) * mm, "end": v(-1530.23, -98.43) * mm});
            skLineSegment(sketch, "E162.left", {"start": v(-1434.98, 98.43) * mm, "end": v(-1434.98, -98.43) * mm});
            skLineSegment(sketch, "E162.right", {"start": v(-1530.23, 98.43) * mm, "end": v(-1530.23, -98.43) * mm});
            skLineSegment(sketch, "E163.1.0", {"start": v(-1498.3, 326.14) * mm, "end": v(-1527.74, 131.5) * mm});
            skLineSegment(sketch, "E163.1.1", {"start": v(-1404.13, 311.9) * mm, "end": v(-1433.57, 117.26) * mm});
            skLineSegment(sketch, "E163.1.2", {"start": v(-1433.57, 117.26) * mm, "end": v(-1527.74, 131.5) * mm});
            skLineSegment(sketch, "E163.1.3", {"start": v(-1404.13, 311.9) * mm, "end": v(-1498.3, 326.14) * mm});
            skLineSegment(sketch, "E163.2.0", {"start": v(-1432.7, 546.53) * mm, "end": v(-1490.9, 358.48) * mm});
            skLineSegment(sketch, "E163.2.1", {"start": v(-1341.7, 518.36) * mm, "end": v(-1399.91, 330.31) * mm});
            skLineSegment(sketch, "E163.2.2", {"start": v(-1399.91, 330.31) * mm, "end": v(-1490.9, 358.48) * mm});
            skLineSegment(sketch, "E163.2.3", {"start": v(-1341.7, 518.36) * mm, "end": v(-1432.7, 546.53) * mm});
            skLineSegment(sketch, "E163.3.0", {"start": v(-1334.86, 754.62) * mm, "end": v(-1420.53, 577.4) * mm});
            skLineSegment(sketch, "E163.3.1", {"start": v(-1249.1, 713.16) * mm, "end": v(-1334.78, 535.93) * mm});
            skLineSegment(sketch, "E163.3.2", {"start": v(-1334.78, 535.93) * mm, "end": v(-1420.53, 577.4) * mm});
            skLineSegment(sketch, "E163.3.3", {"start": v(-1249.1, 713.16) * mm, "end": v(-1334.86, 754.62) * mm});
            skLineSegment(sketch, "E163.4.0", {"start": v(-1207, 945.74) * mm, "end": v(-1318.22, 783.32) * mm});
            skLineSegment(sketch, "E163.4.1", {"start": v(-1128.42, 891.93) * mm, "end": v(-1239.63, 729.5) * mm});
            skLineSegment(sketch, "E163.4.2", {"start": v(-1239.63, 729.5) * mm, "end": v(-1318.22, 783.32) * mm});
            skLineSegment(sketch, "E163.4.3", {"start": v(-1128.42, 891.93) * mm, "end": v(-1207, 945.74) * mm});
            skLineSegment(sketch, "E163.5.0", {"start": v(-1052.02, 1115.6) * mm, "end": v(-1186.27, 971.63) * mm});
            skLineSegment(sketch, "E163.5.1", {"start": v(-982.35, 1050.64) * mm, "end": v(-1116.6, 906.67) * mm});
            skLineSegment(sketch, "E163.5.2", {"start": v(-1116.6, 906.67) * mm, "end": v(-1186.27, 971.63) * mm});
            skLineSegment(sketch, "E163.5.3", {"start": v(-982.35, 1050.64) * mm, "end": v(-1052.02, 1115.6) * mm});
            skLineSegment(sketch, "E163.6.0", {"start": v(-873.37, 1260.37) * mm, "end": v(-1027.64, 1138.1) * mm});
            skLineSegment(sketch, "E163.6.1", {"start": v(-814.2, 1185.72) * mm, "end": v(-968.47, 1063.45) * mm});
            skLineSegment(sketch, "E163.6.2", {"start": v(-968.47, 1063.45) * mm, "end": v(-1027.64, 1138.1) * mm});
            skLineSegment(sketch, "E163.6.3", {"start": v(-814.2, 1185.72) * mm, "end": v(-873.37, 1260.37) * mm});
            skLineSegment(sketch, "E163.7.0", {"start": v(-675.08, 1376.8) * mm, "end": v(-845.9, 1278.97) * mm});
            skLineSegment(sketch, "E163.7.1", {"start": v(-627.74, 1294.14) * mm, "end": v(-798.56, 1196.31) * mm});
            skLineSegment(sketch, "E163.7.2", {"start": v(-798.56, 1196.31) * mm, "end": v(-845.9, 1278.97) * mm});
            skLineSegment(sketch, "E163.7.3", {"start": v(-627.74, 1294.14) * mm, "end": v(-675.08, 1376.8) * mm});
            skLineSegment(sketch, "E163.8.0", {"start": v(-461.6, 1462.26) * mm, "end": v(-645.13, 1391.08) * mm});
            skLineSegment(sketch, "E163.8.1", {"start": v(-427.16, 1373.46) * mm, "end": v(-610.69, 1302.28) * mm});
            skLineSegment(sketch, "E163.8.2", {"start": v(-610.69, 1302.28) * mm, "end": v(-645.13, 1391.08) * mm});
            skLineSegment(sketch, "E163.8.3", {"start": v(-427.16, 1373.46) * mm, "end": v(-461.6, 1462.26) * mm});
            skLineSegment(sketch, "E163.9.0", {"start": v(-237.76, 1514.85) * mm, "end": v(-429.86, 1471.9) * mm});
            skLineSegment(sketch, "E163.9.1", {"start": v(-216.98, 1421.9) * mm, "end": v(-409.09, 1378.95) * mm});
            skLineSegment(sketch, "E163.9.2", {"start": v(-409.09, 1378.95) * mm, "end": v(-429.86, 1471.9) * mm});
            skLineSegment(sketch, "E163.9.3", {"start": v(-216.98, 1421.9) * mm, "end": v(-237.76, 1514.85) * mm});
            skLineSegment(sketch, "E163.10.0", {"start": v(-8.56, 1533.37) * mm, "end": v(-204.93, 1519.64) * mm});
            skLineSegment(sketch, "E163.10.1", {"start": v(-1.91, 1438.35) * mm, "end": v(-198.28, 1424.62) * mm});
            skLineSegment(sketch, "E163.10.2", {"start": v(-198.28, 1424.62) * mm, "end": v(-204.93, 1519.64) * mm});
            skLineSegment(sketch, "E163.10.3", {"start": v(-1.91, 1438.35) * mm, "end": v(-8.56, 1533.37) * mm});
            skLineSegment(sketch, "E163.anchor1", {"start": v(0, 0) * mm, "end": v(-1530.23, -98.43) * mm, "construction": true});
            skLineSegment(sketch, "E163.anchor2", {"start": v(0, 0) * mm, "end": v(-204.93, 1519.64) * mm, "construction": true});
            skLineSegment(sketch, "E164.MirrorCS", {"start": v(-1433.57, -117.26) * mm, "end": v(-1527.74, -131.5) * mm});
            skLineSegment(sketch, "E165.MirrorCS", {"start": v(-1498.3, -326.14) * mm, "end": v(-1527.74, -131.5) * mm});
            skLineSegment(sketch, "E166.MirrorCS", {"start": v(-1404.13, -311.9) * mm, "end": v(-1433.57, -117.26) * mm});
            skLineSegment(sketch, "E167.MirrorCS", {"start": v(-1404.13, -311.9) * mm, "end": v(-1498.3, -326.14) * mm});
            skLineSegment(sketch, "E168.MirrorCS", {"start": v(-1207, -945.74) * mm, "end": v(-1318.22, -783.32) * mm});
            skLineSegment(sketch, "E169.MirrorCS", {"start": v(-461.6, -1462.26) * mm, "end": v(-645.13, -1391.08) * mm});
            skLineSegment(sketch, "E170.MirrorCS", {"start": v(-1052.02, -1115.6) * mm, "end": v(-1186.27, -971.63) * mm});
            skLineSegment(sketch, "E171.MirrorCS", {"start": v(-982.35, -1050.64) * mm, "end": v(-1052.02, -1115.6) * mm});
            skLineSegment(sketch, "E172.MirrorCS", {"start": v(-409.09, -1378.95) * mm, "end": v(-429.86, -1471.9) * mm});
            skLineSegment(sketch, "E173.MirrorCS", {"start": v(-427.16, -1373.46) * mm, "end": v(-461.6, -1462.26) * mm});
            skLineSegment(sketch, "E174.MirrorCS", {"start": v(-968.47, -1063.45) * mm, "end": v(-1027.64, -1138.1) * mm});
            skLineSegment(sketch, "E175.MirrorCS", {"start": v(-1334.86, -754.62) * mm, "end": v(-1420.53, -577.4) * mm});
            skLineSegment(sketch, "E176.MirrorCS", {"start": v(-8.56, -1533.37) * mm, "end": v(-204.93, -1519.64) * mm});
            skLineSegment(sketch, "E177.MirrorCS", {"start": v(-873.37, -1260.37) * mm, "end": v(-1027.64, -1138.1) * mm});
            skLineSegment(sketch, "E178.MirrorCS", {"start": v(-237.76, -1514.85) * mm, "end": v(-429.86, -1471.9) * mm});
            skLineSegment(sketch, "E179.MirrorCS", {"start": v(-216.98, -1421.9) * mm, "end": v(-237.76, -1514.85) * mm});
            skLineSegment(sketch, "E180.MirrorCS", {"start": v(-1.91, -1438.35) * mm, "end": v(-8.56, -1533.37) * mm});
            skLineSegment(sketch, "E181.MirrorCS", {"start": v(-814.2, -1185.72) * mm, "end": v(-873.37, -1260.37) * mm});
            skLineSegment(sketch, "E182.MirrorCS", {"start": v(-1341.7, -518.36) * mm, "end": v(-1432.7, -546.53) * mm});
            skLineSegment(sketch, "E183.MirrorCS", {"start": v(-1399.91, -330.31) * mm, "end": v(-1490.9, -358.48) * mm});
            skLineSegment(sketch, "E184.MirrorCS", {"start": v(-1128.42, -891.93) * mm, "end": v(-1207, -945.74) * mm});
            skLineSegment(sketch, "E185.MirrorCS", {"start": v(-675.08, -1376.8) * mm, "end": v(-845.9, -1278.97) * mm});
            skLineSegment(sketch, "E186.MirrorCS", {"start": v(-1432.7, -546.53) * mm, "end": v(-1490.9, -358.48) * mm});
            skLineSegment(sketch, "E187.MirrorCS", {"start": v(-1116.6, -906.67) * mm, "end": v(-1186.27, -971.63) * mm});
            skLineSegment(sketch, "E188.MirrorCS", {"start": v(-198.28, -1424.62) * mm, "end": v(-204.93, -1519.64) * mm});
            skLineSegment(sketch, "E189.MirrorCS", {"start": v(-1249.1, -713.16) * mm, "end": v(-1334.86, -754.62) * mm});
            skLineSegment(sketch, "E190.MirrorCS", {"start": v(-627.74, -1294.14) * mm, "end": v(-675.08, -1376.8) * mm});
            skLineSegment(sketch, "E191.MirrorCS", {"start": v(-1334.78, -535.93) * mm, "end": v(-1420.53, -577.4) * mm});
            skLineSegment(sketch, "E192.MirrorCS", {"start": v(-1239.63, -729.5) * mm, "end": v(-1318.22, -783.32) * mm});
            skLineSegment(sketch, "E193.MirrorCS", {"start": v(-610.69, -1302.28) * mm, "end": v(-645.13, -1391.08) * mm});
            skLineSegment(sketch, "E194.MirrorCS", {"start": v(-1128.42, -891.93) * mm, "end": v(-1239.63, -729.5) * mm});
            skLineSegment(sketch, "E195.MirrorCS", {"start": v(-798.56, -1196.31) * mm, "end": v(-845.9, -1278.97) * mm});
            skLineSegment(sketch, "E196.MirrorCS", {"start": v(-627.74, -1294.14) * mm, "end": v(-798.56, -1196.31) * mm});
            skLineSegment(sketch, "E197.MirrorCS", {"start": v(0, 0) * mm, "end": v(-204.93, -1519.64) * mm, "construction": true});
            skLineSegment(sketch, "E198.MirrorCS", {"start": v(-1341.7, -518.36) * mm, "end": v(-1399.91, -330.31) * mm});
            skArc(sketch, "E199.MirrorC", {"start": v(-8.56, -1533.37) * mm, "mid": v(-1533.4, 0) * mm, "end": v(-8.56, 1533.37) * mm, "construction": true});
            skLineSegment(sketch, "E200.MirrorCS", {"start": v(-1249.1, -713.16) * mm, "end": v(-1334.78, -535.93) * mm});
            skLineSegment(sketch, "E201.MirrorCS", {"start": v(-1.91, -1438.35) * mm, "end": v(-198.28, -1424.62) * mm});
            skLineSegment(sketch, "E202.MirrorCS", {"start": v(-814.2, -1185.72) * mm, "end": v(-968.47, -1063.45) * mm});
            skLineSegment(sketch, "E203.MirrorCS", {"start": v(-427.16, -1373.46) * mm, "end": v(-610.69, -1302.28) * mm});
            skLineSegment(sketch, "E204.MirrorCS", {"start": v(-216.98, -1421.9) * mm, "end": v(-409.09, -1378.95) * mm});
            skLineSegment(sketch, "E205.MirrorCS", {"start": v(-982.35, -1050.64) * mm, "end": v(-1116.6, -906.67) * mm});
            skSolve(sketch);
        }
        {
            var Q0;
            Q0=qCreatedBy(makeId("Top.planeOp"),FACE);
            var sketch = newSketch(context, id + "F4", { "sketchPlane" : qUnion([Q0])});
            skArc(sketch, "E206", {"start": v(14.15, 1434.91) * mm, "mid": v(-1007.18, 1022.13) * mm, "end": v(-1434.97, 7) * mm});
            skLineSegment(sketch, "E207", {"start": v(-1434.97, 7) * mm, "end": v(-1420.5, 203.31) * mm});
            skLineSegment(sketch, "E208", {"start": v(-1420.5, 203.31) * mm, "end": v(-1325.51, 196.32) * mm});
            skLineSegment(sketch, "E209", {"start": v(-1325.51, 196.32) * mm, "end": v(-1339.97, 0) * mm});
            skLineSegment(sketch, "E210", {"start": v(-1339.97, 0) * mm, "end": v(-1434.97, 7) * mm});
            skLineSegment(sketch, "E211.1.0", {"start": v(-1370.04, 426.8) * mm, "end": v(-1277.37, 404.78) * mm});
            skLineSegment(sketch, "E211.1.1", {"start": v(-1415.56, 235.29) * mm, "end": v(-1370.04, 426.8) * mm});
            skLineSegment(sketch, "E211.1.2", {"start": v(-1277.37, 404.78) * mm, "end": v(-1322.9, 213.26) * mm});
            skLineSegment(sketch, "E211.1.3", {"start": v(-1322.9, 213.26) * mm, "end": v(-1415.56, 235.29) * mm});
            skLineSegment(sketch, "E211.2.0", {"start": v(-1284.65, 639.4) * mm, "end": v(-1196.67, 602.91) * mm});
            skLineSegment(sketch, "E211.2.1", {"start": v(-1360.07, 457.58) * mm, "end": v(-1284.65, 639.4) * mm});
            skLineSegment(sketch, "E211.2.2", {"start": v(-1196.67, 602.91) * mm, "end": v(-1272.1, 421.08) * mm});
            skLineSegment(sketch, "E211.2.3", {"start": v(-1272.1, 421.08) * mm, "end": v(-1360.07, 457.58) * mm});
            skLineSegment(sketch, "E211.3.0", {"start": v(-1166.51, 835.71) * mm, "end": v(-1085.46, 785.68) * mm});
            skLineSegment(sketch, "E211.3.1", {"start": v(-1269.91, 668.2) * mm, "end": v(-1166.51, 835.71) * mm});
            skLineSegment(sketch, "E211.3.2", {"start": v(-1085.46, 785.68) * mm, "end": v(-1188.86, 618.17) * mm});
            skLineSegment(sketch, "E211.3.3", {"start": v(-1188.86, 618.17) * mm, "end": v(-1269.91, 668.2) * mm});
            skLineSegment(sketch, "E211.4.0", {"start": v(-1018.64, 1010.72) * mm, "end": v(-946.58, 948.42) * mm});
            skLineSegment(sketch, "E211.4.1", {"start": v(-1147.38, 861.8) * mm, "end": v(-1018.64, 1010.72) * mm});
            skLineSegment(sketch, "E211.4.2", {"start": v(-946.58, 948.42) * mm, "end": v(-1075.32, 799.5) * mm});
            skLineSegment(sketch, "E211.4.3", {"start": v(-1075.32, 799.5) * mm, "end": v(-1147.38, 861.8) * mm});
            skLineSegment(sketch, "E211.5.0", {"start": v(-844.8, 1159.95) * mm, "end": v(-783.57, 1086.99) * mm});
            skLineSegment(sketch, "E211.5.1", {"start": v(-995.6, 1033.42) * mm, "end": v(-844.8, 1159.95) * mm});
            skLineSegment(sketch, "E211.5.2", {"start": v(-783.57, 1086.99) * mm, "end": v(-934.37, 960.46) * mm});
            skLineSegment(sketch, "E211.5.3", {"start": v(-934.37, 960.46) * mm, "end": v(-995.6, 1033.42) * mm});
            skLineSegment(sketch, "E211.6.0", {"start": v(-649.42, 1279.62) * mm, "end": v(-600.59, 1197.84) * mm});
            skLineSegment(sketch, "E211.6.1", {"start": v(-818.43, 1178.7) * mm, "end": v(-649.42, 1279.62) * mm});
            skLineSegment(sketch, "E211.6.2", {"start": v(-600.59, 1197.84) * mm, "end": v(-769.6, 1096.92) * mm});
            skLineSegment(sketch, "E211.6.3", {"start": v(-769.6, 1096.92) * mm, "end": v(-818.43, 1178.7) * mm});
            skLineSegment(sketch, "E211.7.0", {"start": v(-437.49, 1366.67) * mm, "end": v(-402.3, 1278.16) * mm});
            skLineSegment(sketch, "E211.7.1", {"start": v(-620.4, 1293.93) * mm, "end": v(-437.49, 1366.67) * mm});
            skLineSegment(sketch, "E211.7.2", {"start": v(-402.3, 1278.16) * mm, "end": v(-585.22, 1205.42) * mm});
            skLineSegment(sketch, "E211.7.3", {"start": v(-585.22, 1205.42) * mm, "end": v(-620.4, 1293.93) * mm});
            skLineSegment(sketch, "E211.8.0", {"start": v(-214.4, 1418.87) * mm, "end": v(-193.74, 1325.9) * mm});
            skLineSegment(sketch, "E211.8.1", {"start": v(-406.57, 1376.18) * mm, "end": v(-214.4, 1418.87) * mm});
            skLineSegment(sketch, "E211.8.2", {"start": v(-193.74, 1325.9) * mm, "end": v(-385.9, 1283.2) * mm});
            skLineSegment(sketch, "E211.8.3", {"start": v(-385.9, 1283.2) * mm, "end": v(-406.57, 1376.18) * mm});
            skLineSegment(sketch, "E211.9.0", {"start": v(14.15, 1434.91) * mm, "end": v(19.74, 1339.83) * mm});
            skLineSegment(sketch, "E211.9.1", {"start": v(-182.36, 1423.35) * mm, "end": v(14.15, 1434.91) * mm});
            skLineSegment(sketch, "E211.9.2", {"start": v(19.74, 1339.83) * mm, "end": v(-176.77, 1328.26) * mm});
            skLineSegment(sketch, "E211.9.3", {"start": v(-176.77, 1328.26) * mm, "end": v(-182.36, 1423.35) * mm});
            skLineSegment(sketch, "E211.anchor1", {"start": v(0, 0) * mm, "end": v(-1420.5, 203.31) * mm, "construction": true});
            skLineSegment(sketch, "E211.anchor2", {"start": v(0, 0) * mm, "end": v(14.15, 1434.91) * mm, "construction": true});
            skSolve(sketch);
        }
        {
            var Q0;
            Q0=qCreatedBy(makeId("Top.planeOp"),FACE);
            var sketch = newSketch(context, id + "F5", { "sketchPlane" : qUnion([Q0])});
            skArc(sketch, "E212", {"start": v(0, 1336.35) * mm, "mid": v(-1336.35, 0) * mm, "end": v(0, -1336.35) * mm});
            skLineSegment(sketch, "E213.bottom", {"start": v(-1332.72, 98.43) * mm, "end": v(-1237.47, 98.43) * mm});
            skLineSegment(sketch, "E213.top", {"start": v(-1332.72, -98.43) * mm, "end": v(-1237.47, -98.43) * mm});
            skLineSegment(sketch, "E213.left", {"start": v(-1332.72, 98.43) * mm, "end": v(-1332.72, -98.43) * mm});
            skLineSegment(sketch, "E213.right", {"start": v(-1237.47, 98.43) * mm, "end": v(-1237.47, -98.43) * mm});
            skLineSegment(sketch, "E214", {"start": v(0, 1336.35) * mm, "end": v(0, -1336.35) * mm});
            skLineSegment(sketch, "E215.1.0", {"start": v(-1298.5, 315.78) * mm, "end": v(-1204.55, 300.15) * mm});
            skLineSegment(sketch, "E215.1.1", {"start": v(-1298.5, 315.78) * mm, "end": v(-1330.8, 121.6) * mm});
            skLineSegment(sketch, "E215.1.2", {"start": v(-1330.8, 121.6) * mm, "end": v(-1236.85, 105.97) * mm});
            skLineSegment(sketch, "E215.1.3", {"start": v(-1204.55, 300.15) * mm, "end": v(-1236.85, 105.97) * mm});
            skLineSegment(sketch, "E215.2.0", {"start": v(-1229.09, 524.57) * mm, "end": v(-1138.97, 493.74) * mm});
            skLineSegment(sketch, "E215.2.1", {"start": v(-1229.09, 524.57) * mm, "end": v(-1292.82, 338.32) * mm});
            skLineSegment(sketch, "E215.2.2", {"start": v(-1292.82, 338.32) * mm, "end": v(-1202.7, 307.49) * mm});
            skLineSegment(sketch, "E215.2.3", {"start": v(-1138.97, 493.74) * mm, "end": v(-1202.7, 307.49) * mm});
            skLineSegment(sketch, "E215.3.0", {"start": v(-1126.35, 719.14) * mm, "end": v(-1042.51, 673.94) * mm});
            skLineSegment(sketch, "E215.3.1", {"start": v(-1126.35, 719.14) * mm, "end": v(-1219.78, 545.88) * mm});
            skLineSegment(sketch, "E215.3.2", {"start": v(-1219.78, 545.88) * mm, "end": v(-1135.94, 500.67) * mm});
            skLineSegment(sketch, "E215.3.3", {"start": v(-1042.51, 673.94) * mm, "end": v(-1135.94, 500.67) * mm});
            skLineSegment(sketch, "E215.4.0", {"start": v(-993.08, 894.22) * mm, "end": v(-917.8, 835.87) * mm});
            skLineSegment(sketch, "E215.4.1", {"start": v(-993.08, 894.22) * mm, "end": v(-1113.67, 738.63) * mm});
            skLineSegment(sketch, "E215.4.2", {"start": v(-1113.67, 738.63) * mm, "end": v(-1038.38, 680.28) * mm});
            skLineSegment(sketch, "E215.4.3", {"start": v(-917.8, 835.87) * mm, "end": v(-1038.38, 680.28) * mm});
            skLineSegment(sketch, "E215.5.0", {"start": v(-832.88, 1045.06) * mm, "end": v(-768.2, 975.14) * mm});
            skLineSegment(sketch, "E215.5.1", {"start": v(-832.88, 1045.06) * mm, "end": v(-977.37, 911.36) * mm});
            skLineSegment(sketch, "E215.5.2", {"start": v(-977.37, 911.36) * mm, "end": v(-912.68, 841.45) * mm});
            skLineSegment(sketch, "E215.5.3", {"start": v(-768.2, 975.14) * mm, "end": v(-912.68, 841.45) * mm});
            skLineSegment(sketch, "E215.6.0", {"start": v(-650.11, 1167.56) * mm, "end": v(-597.77, 1087.98) * mm});
            skLineSegment(sketch, "E215.6.1", {"start": v(-650.11, 1167.56) * mm, "end": v(-814.58, 1059.39) * mm});
            skLineSegment(sketch, "E215.6.2", {"start": v(-814.58, 1059.39) * mm, "end": v(-762.24, 979.8) * mm});
            skLineSegment(sketch, "E215.6.3", {"start": v(-597.77, 1087.98) * mm, "end": v(-762.24, 979.8) * mm});
            skLineSegment(sketch, "E215.7.0", {"start": v(-449.71, 1258.41) * mm, "end": v(-411.14, 1171.32) * mm});
            skLineSegment(sketch, "E215.7.1", {"start": v(-449.71, 1258.41) * mm, "end": v(-629.7, 1178.7) * mm});
            skLineSegment(sketch, "E215.7.2", {"start": v(-629.7, 1178.7) * mm, "end": v(-591.13, 1091.6) * mm});
            skLineSegment(sketch, "E215.7.3", {"start": v(-411.14, 1171.32) * mm, "end": v(-591.13, 1091.6) * mm});
            skLineSegment(sketch, "E215.8.0", {"start": v(-237.12, 1315.15) * mm, "end": v(-213.36, 1222.9) * mm});
            skLineSegment(sketch, "E215.8.1", {"start": v(-237.12, 1315.15) * mm, "end": v(-427.75, 1266.04) * mm});
            skLineSegment(sketch, "E215.8.2", {"start": v(-427.75, 1266.04) * mm, "end": v(-404, 1173.8) * mm});
            skLineSegment(sketch, "E215.8.3", {"start": v(-213.36, 1222.9) * mm, "end": v(-404, 1173.8) * mm});
            skLineSegment(sketch, "E215.9.0", {"start": v(-18.1, 1336.23) * mm, "end": v(-9.8, 1241.34) * mm});
            skLineSegment(sketch, "E215.9.1", {"start": v(-18.1, 1336.23) * mm, "end": v(-214.2, 1319.07) * mm});
            skLineSegment(sketch, "E215.9.2", {"start": v(-214.2, 1319.07) * mm, "end": v(-205.9, 1224.19) * mm});
            skLineSegment(sketch, "E215.9.3", {"start": v(-9.8, 1241.34) * mm, "end": v(-205.9, 1224.19) * mm});
            skLineSegment(sketch, "E215.anchor1", {"start": v(0, 0) * mm, "end": v(-1332.72, 98.43) * mm, "construction": true});
            skLineSegment(sketch, "E215.anchor2", {"start": v(0, 0) * mm, "end": v(-18.1, 1336.23) * mm, "construction": true});
            skSolve(sketch);
        }
        {
            var Q0;
            Q0=qCreatedBy(makeId("Top.planeOp"),FACE);
            var sketch = newSketch(context, id + "F6", { "sketchPlane" : qUnion([Q0])});
            skLineSegment(sketch, "E216.bottom", {"start": v(-1826.15, 98.43) * mm, "end": v(-1743.6, 98.43) * mm});
            skLineSegment(sketch, "E216.top", {"start": v(-1826.15, -98.43) * mm, "end": v(-1743.6, -98.43) * mm});
            skLineSegment(sketch, "E216.left", {"start": v(-1826.15, 98.43) * mm, "end": v(-1826.15, -98.43) * mm});
            skLineSegment(sketch, "E216.right", {"start": v(-1743.6, 98.43) * mm, "end": v(-1743.6, -98.43) * mm});
            skSolve(sketch);
        }
        {
            var Q0;
            Q0 = qSketchRegion(id + "F6", true);
            extrude(context, id + "F7", {"entities" : qUnion([Q0]), "depth" : 50.8 * mm, "offsetDistance" : 25.4 * mm});
        }
        {
            var Q0;
            Q0=qCreatedBy(makeId("Right.planeOp"),FACE);
            var sketch = newSketch(context, id + "F8", { "sketchPlane" : qUnion([Q0])});
            skLineSegment(sketch, "E217", {"start": v(0, 0) * mm, "end": v(0, 473.05) * mm});
            skSolve(sketch);
        }
        {
            var Q0;
            Q0=makeQuery(id+"F7.opExtrude","SWEPT_BODY",BODY,{"disambiguationData":[OSD([sQuery(id+"F6.wireOp",EDGE,"E216.bottom"),sQuery(id+"F6.wireOp",EDGE,"E216.top"),sQuery(id+"F6.wireOp",EDGE,"E216.left"),sQuery(id+"F6.wireOp",EDGE,"E216.right")])]});
            var Q1;
            Q1=sQuery(id+"F8.wireOp",EDGE,"E217");
            circularPattern(context, id + "F9", {"entities" : qUnion([Q0]), "axis" : qUnion([Q1]), "angle" : 87 * degree, "instanceCount" : 14, "equalSpace" : true, "isCentered" : true});
        }
        {
            var Q0;
            Q0=qCreatedBy(makeId("Top.planeOp"),FACE);
            var sketch = newSketch(context, id + "F10", { "sketchPlane" : qUnion([Q0])});
            skArc(sketch, "E218", {"start": v(0, 1743.6) * mm, "mid": v(-1743.6, 0) * mm, "end": v(0, -1743.6) * mm, "construction": true});
            skLineSegment(sketch, "E219", {"start": v(0, -1743.6) * mm, "end": v(0, 1743.6) * mm, "construction": true});
            skLineSegment(sketch, "E220.bottom", {"start": v(-1743.11, 41.28) * mm, "end": v(-1546.26, 41.28) * mm});
            skLineSegment(sketch, "E220.top", {"start": v(-1743.11, -41.28) * mm, "end": v(-1546.26, -41.28) * mm});
            skLineSegment(sketch, "E220.left", {"start": v(-1743.11, 41.28) * mm, "end": v(-1743.11, -41.28) * mm});
            skLineSegment(sketch, "E220.right", {"start": v(-1546.26, 41.28) * mm, "end": v(-1546.26, -41.28) * mm});
            skSolve(sketch);
        }
        {
            var Q0;
            Q0 = qSketchRegion(id + "F10", true);
            extrude(context, id + "F11", {"entities" : qUnion([Q0]), "depth" : 50.8 * mm, "offsetDistance" : 25.4 * mm});
        }
        {
            var Q0;
            Q0=makeQuery(id+"F11.opExtrude","SWEPT_BODY",BODY,{"disambiguationData":[OSD([sQuery(id+"F10.wireOp",EDGE,"E220.bottom"),sQuery(id+"F10.wireOp",EDGE,"E220.top"),sQuery(id+"F10.wireOp",EDGE,"E220.left"),sQuery(id+"F10.wireOp",EDGE,"E220.right")])]});
            var Q1;
            Q1=sQuery(id+"F8.wireOp",EDGE,"E217");
            circularPattern(context, id + "F12", {"entities" : qUnion([Q0]), "axis" : qUnion([Q1]), "angle" : 88 * degree, "instanceCount" : 25, "equalSpace" : true, "isCentered" : true});
        }
        {
            var Q0;
            Q0=qCreatedBy(makeId("Top.planeOp"),FACE);
            var sketch = newSketch(context, id + "F13", { "sketchPlane" : qUnion([Q0])});
            skArc(sketch, "E221", {"start": v(0, -1546.26) * mm, "mid": v(-1546.26, 0) * mm, "end": v(0, 1546.26) * mm, "construction": true});
            skLineSegment(sketch, "E222.bottom", {"start": v(-1460.58, 98.43) * mm, "end": v(-1543.13, 98.43) * mm});
            skLineSegment(sketch, "E222.top", {"start": v(-1460.58, -98.43) * mm, "end": v(-1543.13, -98.43) * mm});
            skLineSegment(sketch, "E222.left", {"start": v(-1460.58, 98.43) * mm, "end": v(-1460.58, -98.43) * mm});
            skLineSegment(sketch, "E222.right", {"start": v(-1543.13, 98.43) * mm, "end": v(-1543.13, -98.43) * mm});
            skSolve(sketch);
        }
        {
            var Q0;
            Q0 = qSketchRegion(id + "F13", true);
            extrude(context, id + "F14", {"entities" : qUnion([Q0]), "depth" : 50.8 * mm, "offsetDistance" : 25.4 * mm});
        }
        {
            var Q0;
            Q0=makeQuery(id+"F14.opExtrude","SWEPT_BODY",BODY,{"disambiguationData":[OSD([sQuery(id+"F13.wireOp",EDGE,"E222.bottom"),sQuery(id+"F13.wireOp",EDGE,"E222.top"),sQuery(id+"F13.wireOp",EDGE,"E222.left"),sQuery(id+"F13.wireOp",EDGE,"E222.right")])]});
            var Q1;
            Q1=sQuery(id+"F8.wireOp",EDGE,"E217");
            circularPattern(context, id + "F15", {"entities" : qUnion([Q0]), "axis" : qUnion([Q1]), "angle" : 86 * degree, "instanceCount" : 12, "equalSpace" : true, "isCentered" : true});
        }
        {
            var Q0;
            Q0=qCreatedBy(makeId("Top.planeOp"),FACE);
            var sketch = newSketch(context, id + "F16", { "sketchPlane" : qUnion([Q0])});
            skArc(sketch, "E223", {"start": v(0, -1460.58) * mm, "mid": v(-1460.58, 0) * mm, "end": v(0, 1460.58) * mm, "construction": true});
            skLineSegment(sketch, "E224.bottom", {"start": v(-1460, 41.28) * mm, "end": v(-1263.14, 41.28) * mm});
            skLineSegment(sketch, "E224.top", {"start": v(-1460, -41.28) * mm, "end": v(-1263.14, -41.28) * mm});
            skLineSegment(sketch, "E224.left", {"start": v(-1460, 41.28) * mm, "end": v(-1460, -41.28) * mm});
            skLineSegment(sketch, "E224.right", {"start": v(-1263.14, 41.28) * mm, "end": v(-1263.14, -41.28) * mm});
            skSolve(sketch);
        }
        {
            var Q0;
            Q0=makeQuery(id+"F16.imprint","IMPRINT",FACE,{"disambiguationData":[TD([[makeQuery(id+"F16.imprint","IMPRINT",EDGE,{"derivedFrom":sQuery(id+"F16.wireOp",EDGE,"E224.bottom")}),-1.0]])]});
            extrude(context, id + "F17", {"entities" : qUnion([Q0]), "depth" : 50.8 * mm, "offsetDistance" : 25.4 * mm});
        }
        {
            var Q0;
            Q0=makeQuery(id+"F17.opExtrude","SWEPT_BODY",BODY,{"disambiguationData":[OSD([sQuery(id+"F16.wireOp",EDGE,"E224.bottom"),sQuery(id+"F16.wireOp",EDGE,"E224.top"),sQuery(id+"F16.wireOp",EDGE,"E224.left"),sQuery(id+"F16.wireOp",EDGE,"E224.right")])]});
            var Q1;
            Q1=sQuery(id+"F8.wireOp",EDGE,"E217");
            circularPattern(context, id + "F18", {"entities" : qUnion([Q0]), "axis" : qUnion([Q1]), "angle" : 88 * degree, "instanceCount" : 24, "equalSpace" : true, "isCentered" : true});
        }
        {
            var Q0;
            Q0=qCreatedBy(makeId("Top.planeOp"),FACE);
            var sketch = newSketch(context, id + "F19", { "sketchPlane" : qUnion([Q0])});
            skArc(sketch, "E225", {"start": v(0, -1263.14) * mm, "mid": v(-1263.14, 0) * mm, "end": v(0, 1263.14) * mm, "construction": true});
            skLineSegment(sketch, "E226.bottom", {"start": v(-1259.3, 98.43) * mm, "end": v(-1176.75, 98.43) * mm});
            skLineSegment(sketch, "E226.top", {"start": v(-1259.3, -98.43) * mm, "end": v(-1176.75, -98.43) * mm});
            skLineSegment(sketch, "E226.left", {"start": v(-1259.3, 98.43) * mm, "end": v(-1259.3, -98.43) * mm});
            skLineSegment(sketch, "E226.right", {"start": v(-1176.75, 98.43) * mm, "end": v(-1176.75, -98.43) * mm});
            skSolve(sketch);
        }
        {
            var Q0;
            Q0 = qSketchRegion(id + "F19", true);
            extrude(context, id + "F20", {"entities" : qUnion([Q0]), "depth" : 50.8 * mm, "offsetDistance" : 25.4 * mm});
        }
        {
            var Q0;
            Q0=makeQuery(id+"F20.opExtrude","SWEPT_BODY",BODY,{"disambiguationData":[OSD([sQuery(id+"F19.wireOp",EDGE,"E226.bottom"),sQuery(id+"F19.wireOp",EDGE,"E226.top"),sQuery(id+"F19.wireOp",EDGE,"E226.left"),sQuery(id+"F19.wireOp",EDGE,"E226.right")])]});
            var Q1;
            Q1=sQuery(id+"F8.wireOp",EDGE,"E217");
            circularPattern(context, id + "F21", {"entities" : qUnion([Q0]), "axis" : qUnion([Q1]), "angle" : 85 * degree, "instanceCount" : 9, "equalSpace" : true, "isCentered" : true});
        }
        {
            var Q0;
            Q0=qCreatedBy(makeId("Top.planeOp"),FACE);
            var sketch = newSketch(context, id + "F22", { "sketchPlane" : qUnion([Q0])});
            skArc(sketch, "E227", {"start": v(0, -1176.75) * mm, "mid": v(-1176.75, 0) * mm, "end": v(0, 1176.75) * mm, "construction": true});
            skLineSegment(sketch, "E228.bottom", {"start": v(-1176.03, 41.28) * mm, "end": v(-979.18, 41.28) * mm});
            skLineSegment(sketch, "E228.top", {"start": v(-1176.03, -41.28) * mm, "end": v(-979.18, -41.28) * mm});
            skLineSegment(sketch, "E228.left", {"start": v(-1176.03, 41.28) * mm, "end": v(-1176.03, -41.28) * mm});
            skLineSegment(sketch, "E228.right", {"start": v(-979.18, 41.28) * mm, "end": v(-979.18, -41.28) * mm});
            skSolve(sketch);
        }
        {
            var Q0;
            Q0 = qSketchRegion(id + "F22", true);
            extrude(context, id + "F23", {"entities" : qUnion([Q0]), "depth" : 50.8 * mm, "offsetDistance" : 25.4 * mm});
        }
        {
            var Q0;
            Q0=makeQuery(id+"F23.opExtrude","SWEPT_BODY",BODY,{"disambiguationData":[OSD([sQuery(id+"F22.wireOp",EDGE,"E228.bottom"),sQuery(id+"F22.wireOp",EDGE,"E228.top"),sQuery(id+"F22.wireOp",EDGE,"E228.left"),sQuery(id+"F22.wireOp",EDGE,"E228.right")])]});
            var Q1;
            Q1=sQuery(id+"F8.wireOp",EDGE,"E217");
            circularPattern(context, id + "F24", {"entities" : qUnion([Q0]), "axis" : qUnion([Q1]), "angle" : 88 * degree, "instanceCount" : 18, "equalSpace" : true, "isCentered" : true});
        }
        {
            var Q0;
            Q0=qCreatedBy(makeId("Top.planeOp"),FACE);
            var sketch = newSketch(context, id + "F25", { "sketchPlane" : qUnion([Q0])});
            skArc(sketch, "E229", {"start": v(0, -979.18) * mm, "mid": v(-979.18, 0) * mm, "end": v(0, 979.18) * mm, "construction": true});
            skLineSegment(sketch, "E230.bottom", {"start": v(-974.22, 98.43) * mm, "end": v(-891.67, 98.43) * mm});
            skLineSegment(sketch, "E230.top", {"start": v(-974.22, -98.43) * mm, "end": v(-891.67, -98.43) * mm});
            skLineSegment(sketch, "E230.left", {"start": v(-974.22, 98.43) * mm, "end": v(-974.22, -98.43) * mm});
            skLineSegment(sketch, "E230.right", {"start": v(-891.67, 98.43) * mm, "end": v(-891.67, -98.43) * mm});
            skSolve(sketch);
        }
        {
            var Q0;
            Q0=makeQuery(id+"F25.imprint","IMPRINT",FACE,{"disambiguationData":[TD([[makeQuery(id+"F25.imprint","IMPRINT",EDGE,{"derivedFrom":sQuery(id+"F25.wireOp",EDGE,"E230.bottom")}),-1.0]])]});
            extrude(context, id + "F26", {"entities" : qUnion([Q0]), "depth" : 50.8 * mm, "offsetDistance" : 25.4 * mm});
        }
        {
            var Q0;
            Q0=makeQuery(id+"F26.opExtrude","SWEPT_BODY",BODY,{"disambiguationData":[OSD([sQuery(id+"F25.wireOp",EDGE,"E230.bottom"),sQuery(id+"F25.wireOp",EDGE,"E230.top"),sQuery(id+"F25.wireOp",EDGE,"E230.left"),sQuery(id+"F25.wireOp",EDGE,"E230.right")])]});
            var Q1;
            Q1=sQuery(id+"F8.wireOp",EDGE,"E217");
            circularPattern(context, id + "F27", {"entities" : qUnion([Q0]), "axis" : qUnion([Q1]), "angle" : 83 * degree, "instanceCount" : 7, "equalSpace" : true, "isCentered" : true});
        }
        {
            var Q0;
            Q0=qCreatedBy(makeId("Top.planeOp"),FACE);
            var sketch = newSketch(context, id + "F28", { "sketchPlane" : qUnion([Q0])});
            skArc(sketch, "E231", {"start": v(0, -891.67) * mm, "mid": v(-891.67, 0) * mm, "end": v(0, 891.67) * mm, "construction": true});
            skLineSegment(sketch, "E232.bottom", {"start": v(-890.71, 41.28) * mm, "end": v(-693.86, 41.28) * mm});
            skLineSegment(sketch, "E232.top", {"start": v(-890.71, -41.28) * mm, "end": v(-693.86, -41.28) * mm});
            skLineSegment(sketch, "E232.left", {"start": v(-890.71, 41.28) * mm, "end": v(-890.71, -41.28) * mm});
            skLineSegment(sketch, "E232.right", {"start": v(-693.86, 41.28) * mm, "end": v(-693.86, -41.28) * mm});
            skSolve(sketch);
        }
        {
            var Q0;
            Q0 = qSketchRegion(id + "F28", true);
            extrude(context, id + "F29", {"entities" : qUnion([Q0]), "depth" : 50.8 * mm, "offsetDistance" : 25.4 * mm});
        }
        {
            var Q0;
            Q0=makeQuery(id+"F29.opExtrude","SWEPT_BODY",BODY,{"disambiguationData":[OSD([sQuery(id+"F28.wireOp",EDGE,"E232.bottom"),sQuery(id+"F28.wireOp",EDGE,"E232.top"),sQuery(id+"F28.wireOp",EDGE,"E232.left"),sQuery(id+"F28.wireOp",EDGE,"E232.right")])]});
            var Q1;
            Q1=sQuery(id+"F8.wireOp",EDGE,"E217");
            circularPattern(context, id + "F30", {"entities" : qUnion([Q0]), "axis" : qUnion([Q1]), "angle" : 87 * degree, "instanceCount" : 13, "equalSpace" : true, "isCentered" : true});
        }
        {
            var Q0;
            Q0=qCreatedBy(makeId("Top.planeOp"),FACE);
            var sketch = newSketch(context, id + "F31", { "sketchPlane" : qUnion([Q0])});
            skArc(sketch, "E233", {"start": v(0, -693.86) * mm, "mid": v(-693.86, 0) * mm, "end": v(0, 693.86) * mm, "construction": true});
            skLineSegment(sketch, "E234.bottom", {"start": v(-686.85, 98.43) * mm, "end": v(-604.3, 98.43) * mm});
            skLineSegment(sketch, "E234.top", {"start": v(-686.85, -98.43) * mm, "end": v(-604.3, -98.43) * mm});
            skLineSegment(sketch, "E234.left", {"start": v(-686.85, 98.43) * mm, "end": v(-686.85, -98.43) * mm});
            skLineSegment(sketch, "E234.right", {"start": v(-604.3, 98.43) * mm, "end": v(-604.3, -98.43) * mm});
            skSolve(sketch);
        }
        {
            var Q0;
            Q0=makeQuery(id+"F31.imprint","IMPRINT",FACE,{"disambiguationData":[TD([[makeQuery(id+"F31.imprint","IMPRINT",EDGE,{"derivedFrom":sQuery(id+"F31.wireOp",EDGE,"E234.bottom")}),-1.0]])]});
            extrude(context, id + "F32", {"entities" : qUnion([Q0]), "depth" : 50.8 * mm, "offsetDistance" : 25.4 * mm});
        }
        {
            var Q0;
            Q0=makeQuery(id+"F32.opExtrude","SWEPT_BODY",BODY,{"disambiguationData":[OSD([sQuery(id+"F31.wireOp",EDGE,"E234.bottom"),sQuery(id+"F31.wireOp",EDGE,"E234.top"),sQuery(id+"F31.wireOp",EDGE,"E234.left"),sQuery(id+"F31.wireOp",EDGE,"E234.right")])]});
            var Q1;
            Q1=sQuery(id+"F8.wireOp",EDGE,"E217");
            circularPattern(context, id + "F33", {"entities" : qUnion([Q0]), "axis" : qUnion([Q1]), "angle" : 80 * degree, "instanceCount" : 5, "equalSpace" : true, "isCentered" : true});
        }
        {
            var Q0;
            Q0=qCreatedBy(makeId("Top.planeOp"),FACE);
            var sketch = newSketch(context, id + "F34", { "sketchPlane" : qUnion([Q0])});
            skArc(sketch, "E235", {"start": v(0, -604.3) * mm, "mid": v(-604.3, 0) * mm, "end": v(0, 604.3) * mm, "construction": true});
            skLineSegment(sketch, "E236.bottom", {"start": v(-602.88, 41.28) * mm, "end": v(-406.03, 41.28) * mm});
            skLineSegment(sketch, "E236.top", {"start": v(-602.88, -41.28) * mm, "end": v(-406.03, -41.28) * mm});
            skLineSegment(sketch, "E236.left", {"start": v(-602.88, 41.28) * mm, "end": v(-602.88, -41.28) * mm});
            skLineSegment(sketch, "E236.right", {"start": v(-406.03, 41.28) * mm, "end": v(-406.03, -41.28) * mm});
            skSolve(sketch);
        }
        {
            var Q0;
            Q0=makeQuery(id+"F34.imprint","IMPRINT",FACE,{"disambiguationData":[TD([[makeQuery(id+"F34.imprint","IMPRINT",EDGE,{"derivedFrom":sQuery(id+"F34.wireOp",EDGE,"E236.bottom")}),-1.0]])]});
            extrude(context, id + "F35", {"entities" : qUnion([Q0]), "depth" : 50.8 * mm, "offsetDistance" : 25.4 * mm});
        }
        {
            var Q0;
            Q0=makeQuery(id+"F35.opExtrude","SWEPT_BODY",BODY,{"disambiguationData":[OSD([sQuery(id+"F34.wireOp",EDGE,"E236.bottom"),sQuery(id+"F34.wireOp",EDGE,"E236.top"),sQuery(id+"F34.wireOp",EDGE,"E236.left"),sQuery(id+"F34.wireOp",EDGE,"E236.right")])]});
            var Q1;
            Q1=sQuery(id+"F8.wireOp",EDGE,"E217");
            circularPattern(context, id + "F36", {"entities" : qUnion([Q0]), "axis" : qUnion([Q1]), "angle" : 85 * degree, "instanceCount" : 8, "equalSpace" : true, "isCentered" : true});
        }
        {
            var Q0;
            Q0=qCreatedBy(makeId("Top.planeOp"),FACE);
            var sketch = newSketch(context, id + "F37", { "sketchPlane" : qUnion([Q0])});
            skArc(sketch, "E237", {"start": v(0, -406.03) * mm, "mid": v(-406.03, 0) * mm, "end": v(0, 406.03) * mm, "construction": true});
            skLineSegment(sketch, "E238.bottom", {"start": v(-393.92, 98.43) * mm, "end": v(-311.37, 98.43) * mm});
            skLineSegment(sketch, "E238.top", {"start": v(-393.92, -98.43) * mm, "end": v(-311.37, -98.43) * mm});
            skLineSegment(sketch, "E238.left", {"start": v(-393.92, 98.43) * mm, "end": v(-393.92, -98.43) * mm});
            skLineSegment(sketch, "E238.right", {"start": v(-311.37, 98.43) * mm, "end": v(-311.37, -98.43) * mm});
            skSolve(sketch);
        }
        {
            var Q0;
            Q0 = qSketchRegion(id + "F37", true);
            extrude(context, id + "F38", {"entities" : qUnion([Q0]), "depth" : 50.8 * mm, "offsetDistance" : 25.4 * mm});
        }
        {
            var Q0;
            Q0=makeQuery(id+"F38.opExtrude","SWEPT_BODY",BODY,{"disambiguationData":[OSD([sQuery(id+"F37.wireOp",EDGE,"E238.bottom"),sQuery(id+"F37.wireOp",EDGE,"E238.top"),sQuery(id+"F37.wireOp",EDGE,"E238.left"),sQuery(id+"F37.wireOp",EDGE,"E238.right")])]});
            var Q1;
            Q1=sQuery(id+"F8.wireOp",EDGE,"E217");
            circularPattern(context, id + "F39", {"entities" : qUnion([Q0]), "axis" : qUnion([Q1]), "angle" : 75 * degree, "instanceCount" : 3, "equalSpace" : true, "isCentered" : true});
        }
        {
            var Q0;
            Q0=qCreatedBy(makeId("Top.planeOp"),FACE);
            var sketch = newSketch(context, id + "F40", { "sketchPlane" : qUnion([Q0])});
            skArc(sketch, "E239", {"start": v(0, -311.37) * mm, "mid": v(-311.37, 0) * mm, "end": v(0, 311.37) * mm, "construction": true});
            skLineSegment(sketch, "E240.bottom", {"start": v(-308.63, 41.28) * mm, "end": v(-111.78, 41.28) * mm});
            skLineSegment(sketch, "E240.top", {"start": v(-308.63, -41.28) * mm, "end": v(-111.78, -41.28) * mm});
            skLineSegment(sketch, "E240.left", {"start": v(-308.63, 41.28) * mm, "end": v(-308.63, -41.28) * mm});
            skLineSegment(sketch, "E240.right", {"start": v(-111.78, 41.28) * mm, "end": v(-111.78, -41.28) * mm});
            skSolve(sketch);
        }
        {
            var Q0;
            Q0 = qSketchRegion(id + "F40", true);
            extrude(context, id + "F41", {"entities" : qUnion([Q0]), "depth" : 50.8 * mm, "offsetDistance" : 25.4 * mm});
        }
        {
            var Q0;
            Q0=makeQuery(id+"F41.opExtrude","SWEPT_BODY",BODY,{"disambiguationData":[OSD([sQuery(id+"F40.wireOp",EDGE,"E240.bottom"),sQuery(id+"F40.wireOp",EDGE,"E240.top"),sQuery(id+"F40.wireOp",EDGE,"E240.left"),sQuery(id+"F40.wireOp",EDGE,"E240.right")])]});
            var Q1;
            Q1=sQuery(id+"F8.wireOp",EDGE,"E217");
            circularPattern(context, id + "F42", {"entities" : qUnion([Q0]), "axis" : qUnion([Q1]), "angle" : 90 * degree, "instanceCount" : 3, "equalSpace" : true, "isCentered" : true});
        }
        {
            var Q0;
            Q0=qCreatedBy(makeId("Top.planeOp"),FACE);
            var sketch = newSketch(context, id + "F43", { "sketchPlane" : qUnion([Q0])});
            skLineSegment(sketch, "E241.bottom", {"start": v(-41.28, 98.43) * mm, "end": v(41.28, 98.43) * mm});
            skLineSegment(sketch, "E241.top", {"start": v(-41.28, -98.43) * mm, "end": v(41.28, -98.43) * mm});
            skLineSegment(sketch, "E241.left", {"start": v(-41.28, 98.43) * mm, "end": v(-41.28, -98.43) * mm});
            skLineSegment(sketch, "E241.right", {"start": v(41.28, 98.43) * mm, "end": v(41.28, -98.43) * mm});
            skLineSegment(sketch, "E242", {"start": v(-41.28, 0) * mm, "end": v(41.28, 0) * mm, "construction": true});
            skSolve(sketch);
        }
        {
            var Q0;
            Q0 = qSketchRegion(id + "F43", true);
            extrude(context, id + "F44", {"entities" : qUnion([Q0]), "depth" : 50.8 * mm, "offsetDistance" : 25.4 * mm});
        }
    });
